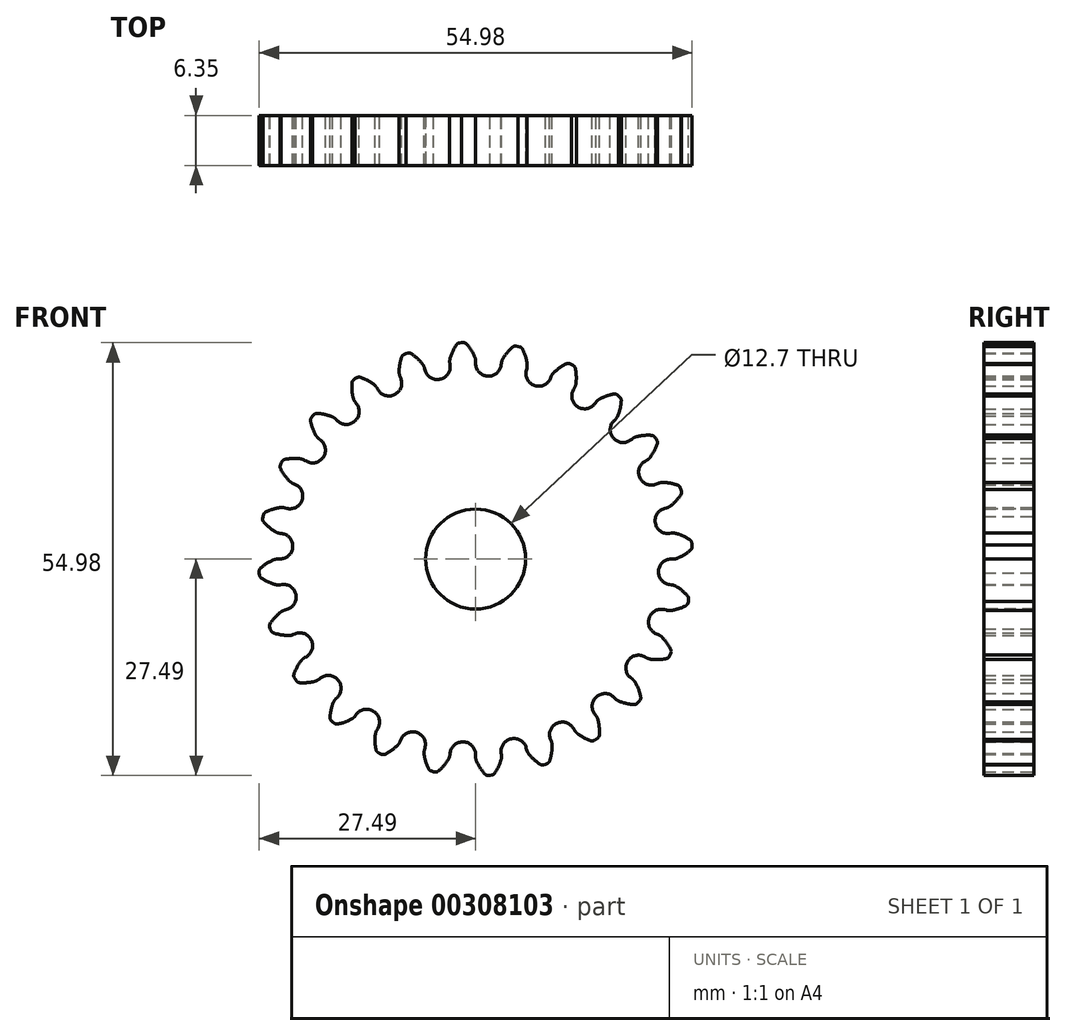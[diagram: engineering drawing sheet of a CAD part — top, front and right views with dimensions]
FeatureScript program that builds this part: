
annotation { "Feature Type Name" : "Feature", "Feature Type Description" : "" }
export const myFeature = defineFeature(function(context is Context, id is Id, definition is map)
    precondition{}
    {
        {
            var Q0;
            Q0=qCreatedBy(makeId("Front.planeOp"),FACE);
            var sketch = newSketch(context, id + "F0", { "sketchPlane" : qUnion([Q0])});
            skArc(sketch, "E0", {"start": v(-4.52, 22.84) * mm, "mid": v(-4.54, 22.84) * mm, "end": v(-4.56, 22.83) * mm});
            skArc(sketch, "E1.trimOffspring", {"start": v(-0.14, 25.74) * mm, "mid": v(-0.59, 26.56) * mm, "end": v(-1.15, 27.31) * mm});
            skLineSegment(sketch, "E2", {"start": v(0, 25.08) * mm, "end": v(0, 24.83) * mm});
            skLineSegment(sketch, "E3", {"start": v(-1.53, 27.49) * mm, "end": v(-1.8, 27.49) * mm});
            skLineSegment(sketch, "E4.MirrorCS", {"start": v(-2.07, 27.45) * mm, "end": v(-1.8, 27.49) * mm});
            skArc(sketch, "E5.MirrorCS", {"start": v(-3.22, 25.54) * mm, "mid": v(-2.89, 26.41) * mm, "end": v(-2.42, 27.23) * mm});
            skLineSegment(sketch, "E6.MirrorCS", {"start": v(-3.28, 24.87) * mm, "end": v(-3.25, 24.62) * mm});
            skPoint(sketch, "E7.orphan", {"position": v(-3, 22.68) * mm});
            skPoint(sketch, "E8.orphan", {"position": v(0, 22.88) * mm});
            skPoint(sketch, "E9.visualSharp", {"position": v(-1.3, 27.49) * mm});
            skArc(sketch, "E9.filletArc", {"start": v(-1.15, 27.31) * mm, "mid": v(-1.32, 27.44) * mm, "end": v(-1.53, 27.49) * mm});
            skPoint(sketch, "E10.visualSharp", {"position": v(-2.3, 27.42) * mm});
            skArc(sketch, "E10.filletArc", {"start": v(-2.07, 27.45) * mm, "mid": v(-2.27, 27.38) * mm, "end": v(-2.42, 27.23) * mm});
            skPoint(sketch, "E11.visualSharp", {"position": v(-3.32, 25.18) * mm});
            skArc(sketch, "E11.filletArc", {"start": v(-3.22, 25.54) * mm, "mid": v(-3.29, 25.2) * mm, "end": v(-3.28, 24.87) * mm});
            skPoint(sketch, "E12.visualSharp", {"position": v(0, 25.4) * mm});
            skArc(sketch, "E12.filletArc", {"start": v(0, 25.08) * mm, "mid": v(-0.03, 25.42) * mm, "end": v(-0.14, 25.74) * mm});
            skPoint(sketch, "E13.visualSharp", {"position": v(0, 23.28) * mm});
            skArc(sketch, "E13.filletArc", {"start": v(0, 24.83) * mm, "mid": v(0.44, 23.74) * mm, "end": v(1.5, 23.23) * mm});
            skPoint(sketch, "E14.visualSharp", {"position": v(-3.04, 23.08) * mm});
            skArc(sketch, "E14.filletArc", {"start": v(-4.52, 22.84) * mm, "mid": v(-3.53, 23.48) * mm, "end": v(-3.25, 24.62) * mm});
            skArc(sketch, "E15.1.0", {"start": v(-10.28, 20.9) * mm, "mid": v(-9.49, 21.76) * mm, "end": v(-9.5, 22.94) * mm});
            skLineSegment(sketch, "E15.1.1", {"start": v(-9.6, 23.17) * mm, "end": v(-9.5, 22.94) * mm});
            skArc(sketch, "E15.1.2", {"start": v(-9.72, 23.83) * mm, "mid": v(-9.7, 23.5) * mm, "end": v(-9.6, 23.17) * mm});
            skArc(sketch, "E15.1.3", {"start": v(-9.72, 23.83) * mm, "mid": v(-9.62, 24.77) * mm, "end": v(-9.39, 25.67) * mm});
            skArc(sketch, "E15.1.4", {"start": v(-9.1, 25.98) * mm, "mid": v(-9.28, 25.86) * mm, "end": v(-9.39, 25.67) * mm});
            skLineSegment(sketch, "E15.1.5", {"start": v(-9.1, 25.98) * mm, "end": v(-8.85, 26.08) * mm});
            skLineSegment(sketch, "E15.1.6", {"start": v(-8.6, 26.15) * mm, "end": v(-8.85, 26.08) * mm});
            skArc(sketch, "E15.1.7", {"start": v(-8.18, 26.08) * mm, "mid": v(-8.38, 26.16) * mm, "end": v(-8.6, 26.15) * mm});
            skArc(sketch, "E15.1.8", {"start": v(-6.8, 24.83) * mm, "mid": v(-7.44, 25.5) * mm, "end": v(-8.18, 26.08) * mm});
            skArc(sketch, "E15.1.9", {"start": v(-6.49, 24.23) * mm, "mid": v(-6.6, 24.54) * mm, "end": v(-6.8, 24.83) * mm});
            skLineSegment(sketch, "E15.1.10", {"start": v(-6.49, 24.23) * mm, "end": v(-6.42, 23.99) * mm});
            skArc(sketch, "E15.1.11", {"start": v(-6.42, 23.99) * mm, "mid": v(-5.72, 23.04) * mm, "end": v(-4.56, 22.83) * mm});
            skArc(sketch, "E15.2.0", {"start": v(-15.34, 17.52) * mm, "mid": v(-14.8, 18.57) * mm, "end": v(-15.12, 19.7) * mm});
            skLineSegment(sketch, "E15.2.1", {"start": v(-15.27, 19.9) * mm, "end": v(-15.12, 19.7) * mm});
            skArc(sketch, "E15.2.2", {"start": v(-15.56, 20.5) * mm, "mid": v(-15.45, 20.18) * mm, "end": v(-15.27, 19.9) * mm});
            skArc(sketch, "E15.2.3", {"start": v(-15.56, 20.5) * mm, "mid": v(-15.7, 21.43) * mm, "end": v(-15.71, 22.37) * mm});
            skArc(sketch, "E15.2.4", {"start": v(-15.52, 22.74) * mm, "mid": v(-15.65, 22.58) * mm, "end": v(-15.71, 22.37) * mm});
            skLineSegment(sketch, "E15.2.5", {"start": v(-15.52, 22.74) * mm, "end": v(-15.3, 22.9) * mm});
            skLineSegment(sketch, "E15.2.6", {"start": v(-15.07, 23.04) * mm, "end": v(-15.3, 22.9) * mm});
            skArc(sketch, "E15.2.7", {"start": v(-14.65, 23.08) * mm, "mid": v(-14.87, 23.1) * mm, "end": v(-15.07, 23.04) * mm});
            skArc(sketch, "E15.2.8", {"start": v(-12.99, 22.22) * mm, "mid": v(-13.79, 22.71) * mm, "end": v(-14.65, 23.08) * mm});
            skArc(sketch, "E15.2.9", {"start": v(-12.54, 21.72) * mm, "mid": v(-12.74, 22) * mm, "end": v(-12.99, 22.22) * mm});
            skLineSegment(sketch, "E15.2.10", {"start": v(-12.54, 21.72) * mm, "end": v(-12.41, 21.5) * mm});
            skArc(sketch, "E15.2.11", {"start": v(-12.41, 21.5) * mm, "mid": v(-11.49, 20.78) * mm, "end": v(-10.32, 20.87) * mm});
            skArc(sketch, "E15.3.0", {"start": v(-19.35, 12.95) * mm, "mid": v(-19.1, 14.1) * mm, "end": v(-19.7, 15.11) * mm});
            skLineSegment(sketch, "E15.3.1", {"start": v(-19.9, 15.26) * mm, "end": v(-19.7, 15.11) * mm});
            skArc(sketch, "E15.3.2", {"start": v(-20.34, 15.78) * mm, "mid": v(-20.15, 15.5) * mm, "end": v(-19.9, 15.26) * mm});
            skArc(sketch, "E15.3.3", {"start": v(-20.34, 15.78) * mm, "mid": v(-20.72, 16.64) * mm, "end": v(-20.97, 17.54) * mm});
            skArc(sketch, "E15.3.4", {"start": v(-20.87, 17.95) * mm, "mid": v(-20.96, 17.75) * mm, "end": v(-20.97, 17.54) * mm});
            skLineSegment(sketch, "E15.3.5", {"start": v(-20.87, 17.95) * mm, "end": v(-20.7, 18.16) * mm});
            skLineSegment(sketch, "E15.3.6", {"start": v(-20.52, 18.35) * mm, "end": v(-20.7, 18.16) * mm});
            skArc(sketch, "E15.3.7", {"start": v(-20.13, 18.5) * mm, "mid": v(-20.34, 18.47) * mm, "end": v(-20.52, 18.35) * mm});
            skArc(sketch, "E15.3.8", {"start": v(-18.3, 18.1) * mm, "mid": v(-19.2, 18.37) * mm, "end": v(-20.13, 18.5) * mm});
            skArc(sketch, "E15.3.9", {"start": v(-17.73, 17.74) * mm, "mid": v(-18, 17.95) * mm, "end": v(-18.3, 18.1) * mm});
            skLineSegment(sketch, "E15.3.10", {"start": v(-17.73, 17.74) * mm, "end": v(-17.55, 17.56) * mm});
            skArc(sketch, "E15.3.11", {"start": v(-17.55, 17.56) * mm, "mid": v(-16.47, 17.1) * mm, "end": v(-15.37, 17.5) * mm});
            skArc(sketch, "E15.4.0", {"start": v(-22.04, 7.5) * mm, "mid": v(-22.1, 8.68) * mm, "end": v(-22.94, 9.5) * mm});
            skLineSegment(sketch, "E15.4.1", {"start": v(-23.17, 9.6) * mm, "end": v(-22.94, 9.5) * mm});
            skArc(sketch, "E15.4.2", {"start": v(-23.73, 9.98) * mm, "mid": v(-23.47, 9.76) * mm, "end": v(-23.17, 9.6) * mm});
            skArc(sketch, "E15.4.3", {"start": v(-23.73, 9.98) * mm, "mid": v(-24.32, 10.7) * mm, "end": v(-24.8, 11.52) * mm});
            skArc(sketch, "E15.4.4", {"start": v(-24.8, 11.93) * mm, "mid": v(-24.85, 11.72) * mm, "end": v(-24.8, 11.52) * mm});
            skLineSegment(sketch, "E15.4.5", {"start": v(-24.8, 11.93) * mm, "end": v(-24.7, 12.18) * mm});
            skLineSegment(sketch, "E15.4.6", {"start": v(-24.57, 12.42) * mm, "end": v(-24.7, 12.18) * mm});
            skArc(sketch, "E15.4.7", {"start": v(-24.23, 12.66) * mm, "mid": v(-24.43, 12.57) * mm, "end": v(-24.57, 12.42) * mm});
            skArc(sketch, "E15.4.8", {"start": v(-22.36, 12.75) * mm, "mid": v(-23.3, 12.78) * mm, "end": v(-24.23, 12.66) * mm});
            skArc(sketch, "E15.4.9", {"start": v(-21.72, 12.55) * mm, "mid": v(-22.03, 12.68) * mm, "end": v(-22.36, 12.75) * mm});
            skLineSegment(sketch, "E15.4.10", {"start": v(-21.72, 12.55) * mm, "end": v(-21.5, 12.42) * mm});
            skArc(sketch, "E15.4.11", {"start": v(-21.5, 12.42) * mm, "mid": v(-20.34, 12.25) * mm, "end": v(-19.37, 12.92) * mm});
            skArc(sketch, "E15.5.0", {"start": v(-23.23, 1.54) * mm, "mid": v(-23.6, 2.66) * mm, "end": v(-24.62, 3.24) * mm});
            skLineSegment(sketch, "E15.5.1", {"start": v(-24.87, 3.27) * mm, "end": v(-24.62, 3.24) * mm});
            skArc(sketch, "E15.5.2", {"start": v(-25.5, 3.5) * mm, "mid": v(-25.2, 3.35) * mm, "end": v(-24.87, 3.27) * mm});
            skArc(sketch, "E15.5.3", {"start": v(-25.5, 3.5) * mm, "mid": v(-26.26, 4.05) * mm, "end": v(-26.93, 4.7) * mm});
            skArc(sketch, "E15.5.4", {"start": v(-27.05, 5.1) * mm, "mid": v(-27.03, 4.9) * mm, "end": v(-26.93, 4.7) * mm});
            skLineSegment(sketch, "E15.5.5", {"start": v(-27.05, 5.1) * mm, "end": v(-27.02, 5.37) * mm});
            skLineSegment(sketch, "E15.5.6", {"start": v(-26.95, 5.63) * mm, "end": v(-27.02, 5.37) * mm});
            skArc(sketch, "E15.5.7", {"start": v(-26.68, 5.96) * mm, "mid": v(-26.85, 5.82) * mm, "end": v(-26.95, 5.63) * mm});
            skArc(sketch, "E15.5.8", {"start": v(-24.9, 6.53) * mm, "mid": v(-25.81, 6.3) * mm, "end": v(-26.68, 5.96) * mm});
            skArc(sketch, "E15.5.9", {"start": v(-24.22, 6.5) * mm, "mid": v(-24.56, 6.55) * mm, "end": v(-24.9, 6.53) * mm});
            skLineSegment(sketch, "E15.5.10", {"start": v(-24.22, 6.5) * mm, "end": v(-23.98, 6.43) * mm});
            skArc(sketch, "E15.5.11", {"start": v(-23.98, 6.43) * mm, "mid": v(-22.81, 6.57) * mm, "end": v(-22.05, 7.47) * mm});
            skArc(sketch, "E15.6.0", {"start": v(-22.84, -4.52) * mm, "mid": v(-23.48, -3.53) * mm, "end": v(-24.62, -3.25) * mm});
            skLineSegment(sketch, "E15.6.1", {"start": v(-24.87, -3.28) * mm, "end": v(-24.62, -3.25) * mm});
            skArc(sketch, "E15.6.2", {"start": v(-25.54, -3.22) * mm, "mid": v(-25.2, -3.29) * mm, "end": v(-24.87, -3.28) * mm});
            skArc(sketch, "E15.6.3", {"start": v(-25.54, -3.22) * mm, "mid": v(-26.41, -2.89) * mm, "end": v(-27.23, -2.42) * mm});
            skArc(sketch, "E15.6.4", {"start": v(-27.45, -2.07) * mm, "mid": v(-27.38, -2.27) * mm, "end": v(-27.23, -2.42) * mm});
            skLineSegment(sketch, "E15.6.5", {"start": v(-27.45, -2.07) * mm, "end": v(-27.49, -1.8) * mm});
            skLineSegment(sketch, "E15.6.6", {"start": v(-27.49, -1.53) * mm, "end": v(-27.49, -1.8) * mm});
            skArc(sketch, "E15.6.7", {"start": v(-27.31, -1.15) * mm, "mid": v(-27.44, -1.32) * mm, "end": v(-27.49, -1.53) * mm});
            skArc(sketch, "E15.6.8", {"start": v(-25.74, -0.14) * mm, "mid": v(-26.56, -0.59) * mm, "end": v(-27.31, -1.15) * mm});
            skArc(sketch, "E15.6.9", {"start": v(-25.08, 0) * mm, "mid": v(-25.42, -0.03) * mm, "end": v(-25.74, -0.14) * mm});
            skLineSegment(sketch, "E15.6.10", {"start": v(-25.08, 0) * mm, "end": v(-24.83, 0) * mm});
            skArc(sketch, "E15.6.11", {"start": v(-24.83, 0) * mm, "mid": v(-23.74, 0.44) * mm, "end": v(-23.23, 1.5) * mm});
            skArc(sketch, "E15.7.0", {"start": v(-20.9, -10.28) * mm, "mid": v(-21.76, -9.49) * mm, "end": v(-22.94, -9.5) * mm});
            skLineSegment(sketch, "E15.7.1", {"start": v(-23.17, -9.6) * mm, "end": v(-22.94, -9.5) * mm});
            skArc(sketch, "E15.7.2", {"start": v(-23.83, -9.72) * mm, "mid": v(-23.5, -9.7) * mm, "end": v(-23.17, -9.6) * mm});
            skArc(sketch, "E15.7.3", {"start": v(-23.83, -9.72) * mm, "mid": v(-24.77, -9.62) * mm, "end": v(-25.67, -9.39) * mm});
            skArc(sketch, "E15.7.4", {"start": v(-25.98, -9.1) * mm, "mid": v(-25.86, -9.28) * mm, "end": v(-25.67, -9.39) * mm});
            skLineSegment(sketch, "E15.7.5", {"start": v(-25.98, -9.1) * mm, "end": v(-26.08, -8.85) * mm});
            skLineSegment(sketch, "E15.7.6", {"start": v(-26.15, -8.6) * mm, "end": v(-26.08, -8.85) * mm});
            skArc(sketch, "E15.7.7", {"start": v(-26.08, -8.18) * mm, "mid": v(-26.16, -8.38) * mm, "end": v(-26.15, -8.6) * mm});
            skArc(sketch, "E15.7.8", {"start": v(-24.83, -6.8) * mm, "mid": v(-25.5, -7.44) * mm, "end": v(-26.08, -8.18) * mm});
            skArc(sketch, "E15.7.9", {"start": v(-24.23, -6.49) * mm, "mid": v(-24.54, -6.6) * mm, "end": v(-24.83, -6.8) * mm});
            skLineSegment(sketch, "E15.7.10", {"start": v(-24.23, -6.49) * mm, "end": v(-23.99, -6.42) * mm});
            skArc(sketch, "E15.7.11", {"start": v(-23.99, -6.42) * mm, "mid": v(-23.04, -5.72) * mm, "end": v(-22.83, -4.56) * mm});
            skArc(sketch, "E15.8.0", {"start": v(-17.52, -15.34) * mm, "mid": v(-18.57, -14.8) * mm, "end": v(-19.7, -15.12) * mm});
            skLineSegment(sketch, "E15.8.1", {"start": v(-19.9, -15.27) * mm, "end": v(-19.7, -15.12) * mm});
            skArc(sketch, "E15.8.2", {"start": v(-20.5, -15.56) * mm, "mid": v(-20.18, -15.45) * mm, "end": v(-19.9, -15.27) * mm});
            skArc(sketch, "E15.8.3", {"start": v(-20.5, -15.56) * mm, "mid": v(-21.43, -15.7) * mm, "end": v(-22.37, -15.71) * mm});
            skArc(sketch, "E15.8.4", {"start": v(-22.74, -15.52) * mm, "mid": v(-22.58, -15.65) * mm, "end": v(-22.37, -15.71) * mm});
            skLineSegment(sketch, "E15.8.5", {"start": v(-22.74, -15.52) * mm, "end": v(-22.9, -15.3) * mm});
            skLineSegment(sketch, "E15.8.6", {"start": v(-23.04, -15.07) * mm, "end": v(-22.9, -15.3) * mm});
            skArc(sketch, "E15.8.7", {"start": v(-23.08, -14.65) * mm, "mid": v(-23.1, -14.87) * mm, "end": v(-23.04, -15.07) * mm});
            skArc(sketch, "E15.8.8", {"start": v(-22.22, -12.99) * mm, "mid": v(-22.71, -13.79) * mm, "end": v(-23.08, -14.65) * mm});
            skArc(sketch, "E15.8.9", {"start": v(-21.72, -12.54) * mm, "mid": v(-22, -12.74) * mm, "end": v(-22.22, -12.99) * mm});
            skLineSegment(sketch, "E15.8.10", {"start": v(-21.72, -12.54) * mm, "end": v(-21.5, -12.41) * mm});
            skArc(sketch, "E15.8.11", {"start": v(-21.5, -12.41) * mm, "mid": v(-20.78, -11.49) * mm, "end": v(-20.87, -10.32) * mm});
            skArc(sketch, "E15.9.0", {"start": v(-12.95, -19.35) * mm, "mid": v(-14.1, -19.1) * mm, "end": v(-15.11, -19.7) * mm});
            skLineSegment(sketch, "E15.9.1", {"start": v(-15.26, -19.9) * mm, "end": v(-15.11, -19.7) * mm});
            skArc(sketch, "E15.9.2", {"start": v(-15.78, -20.34) * mm, "mid": v(-15.5, -20.15) * mm, "end": v(-15.26, -19.9) * mm});
            skArc(sketch, "E15.9.3", {"start": v(-15.78, -20.34) * mm, "mid": v(-16.64, -20.72) * mm, "end": v(-17.54, -20.97) * mm});
            skArc(sketch, "E15.9.4", {"start": v(-17.95, -20.87) * mm, "mid": v(-17.75, -20.96) * mm, "end": v(-17.54, -20.97) * mm});
            skLineSegment(sketch, "E15.9.5", {"start": v(-17.95, -20.87) * mm, "end": v(-18.16, -20.7) * mm});
            skLineSegment(sketch, "E15.9.6", {"start": v(-18.35, -20.52) * mm, "end": v(-18.16, -20.7) * mm});
            skArc(sketch, "E15.9.7", {"start": v(-18.5, -20.13) * mm, "mid": v(-18.47, -20.34) * mm, "end": v(-18.35, -20.52) * mm});
            skArc(sketch, "E15.9.8", {"start": v(-18.1, -18.3) * mm, "mid": v(-18.37, -19.2) * mm, "end": v(-18.5, -20.13) * mm});
            skArc(sketch, "E15.9.9", {"start": v(-17.74, -17.73) * mm, "mid": v(-17.95, -18) * mm, "end": v(-18.1, -18.3) * mm});
            skLineSegment(sketch, "E15.9.10", {"start": v(-17.74, -17.73) * mm, "end": v(-17.56, -17.55) * mm});
            skArc(sketch, "E15.9.11", {"start": v(-17.56, -17.55) * mm, "mid": v(-17.1, -16.47) * mm, "end": v(-17.5, -15.37) * mm});
            skArc(sketch, "E15.10.0", {"start": v(-7.5, -22.04) * mm, "mid": v(-8.68, -22.1) * mm, "end": v(-9.5, -22.94) * mm});
            skLineSegment(sketch, "E15.10.1", {"start": v(-9.6, -23.17) * mm, "end": v(-9.5, -22.94) * mm});
            skArc(sketch, "E15.10.2", {"start": v(-9.98, -23.73) * mm, "mid": v(-9.76, -23.47) * mm, "end": v(-9.6, -23.17) * mm});
            skArc(sketch, "E15.10.3", {"start": v(-9.98, -23.73) * mm, "mid": v(-10.7, -24.32) * mm, "end": v(-11.52, -24.8) * mm});
            skArc(sketch, "E15.10.4", {"start": v(-11.93, -24.8) * mm, "mid": v(-11.72, -24.85) * mm, "end": v(-11.52, -24.8) * mm});
            skLineSegment(sketch, "E15.10.5", {"start": v(-11.93, -24.8) * mm, "end": v(-12.18, -24.7) * mm});
            skLineSegment(sketch, "E15.10.6", {"start": v(-12.42, -24.57) * mm, "end": v(-12.18, -24.7) * mm});
            skArc(sketch, "E15.10.7", {"start": v(-12.66, -24.23) * mm, "mid": v(-12.57, -24.43) * mm, "end": v(-12.42, -24.57) * mm});
            skArc(sketch, "E15.10.8", {"start": v(-12.75, -22.36) * mm, "mid": v(-12.78, -23.3) * mm, "end": v(-12.66, -24.23) * mm});
            skArc(sketch, "E15.10.9", {"start": v(-12.55, -21.72) * mm, "mid": v(-12.68, -22.03) * mm, "end": v(-12.75, -22.36) * mm});
            skLineSegment(sketch, "E15.10.10", {"start": v(-12.55, -21.72) * mm, "end": v(-12.42, -21.5) * mm});
            skArc(sketch, "E15.10.11", {"start": v(-12.42, -21.5) * mm, "mid": v(-12.25, -20.34) * mm, "end": v(-12.92, -19.37) * mm});
            skArc(sketch, "E15.11.0", {"start": v(-1.54, -23.23) * mm, "mid": v(-2.66, -23.6) * mm, "end": v(-3.24, -24.62) * mm});
            skLineSegment(sketch, "E15.11.1", {"start": v(-3.27, -24.87) * mm, "end": v(-3.24, -24.62) * mm});
            skArc(sketch, "E15.11.2", {"start": v(-3.5, -25.5) * mm, "mid": v(-3.35, -25.2) * mm, "end": v(-3.27, -24.87) * mm});
            skArc(sketch, "E15.11.3", {"start": v(-3.5, -25.5) * mm, "mid": v(-4.05, -26.26) * mm, "end": v(-4.7, -26.93) * mm});
            skArc(sketch, "E15.11.4", {"start": v(-5.1, -27.05) * mm, "mid": v(-4.9, -27.03) * mm, "end": v(-4.7, -26.93) * mm});
            skLineSegment(sketch, "E15.11.5", {"start": v(-5.1, -27.05) * mm, "end": v(-5.37, -27.02) * mm});
            skLineSegment(sketch, "E15.11.6", {"start": v(-5.63, -26.95) * mm, "end": v(-5.37, -27.02) * mm});
            skArc(sketch, "E15.11.7", {"start": v(-5.96, -26.68) * mm, "mid": v(-5.82, -26.85) * mm, "end": v(-5.63, -26.95) * mm});
            skArc(sketch, "E15.11.8", {"start": v(-6.53, -24.9) * mm, "mid": v(-6.3, -25.81) * mm, "end": v(-5.96, -26.68) * mm});
            skArc(sketch, "E15.11.9", {"start": v(-6.5, -24.22) * mm, "mid": v(-6.55, -24.56) * mm, "end": v(-6.53, -24.9) * mm});
            skLineSegment(sketch, "E15.11.10", {"start": v(-6.5, -24.22) * mm, "end": v(-6.43, -23.98) * mm});
            skArc(sketch, "E15.11.11", {"start": v(-6.43, -23.98) * mm, "mid": v(-6.57, -22.81) * mm, "end": v(-7.47, -22.05) * mm});
            skArc(sketch, "E15.12.0", {"start": v(4.52, -22.84) * mm, "mid": v(3.53, -23.48) * mm, "end": v(3.25, -24.62) * mm});
            skLineSegment(sketch, "E15.12.1", {"start": v(3.28, -24.87) * mm, "end": v(3.25, -24.62) * mm});
            skArc(sketch, "E15.12.2", {"start": v(3.22, -25.54) * mm, "mid": v(3.29, -25.2) * mm, "end": v(3.28, -24.87) * mm});
            skArc(sketch, "E15.12.3", {"start": v(3.22, -25.54) * mm, "mid": v(2.89, -26.41) * mm, "end": v(2.42, -27.23) * mm});
            skArc(sketch, "E15.12.4", {"start": v(2.07, -27.45) * mm, "mid": v(2.27, -27.38) * mm, "end": v(2.42, -27.23) * mm});
            skLineSegment(sketch, "E15.12.5", {"start": v(2.07, -27.45) * mm, "end": v(1.8, -27.49) * mm});
            skLineSegment(sketch, "E15.12.6", {"start": v(1.53, -27.49) * mm, "end": v(1.8, -27.49) * mm});
            skArc(sketch, "E15.12.7", {"start": v(1.15, -27.31) * mm, "mid": v(1.32, -27.44) * mm, "end": v(1.53, -27.49) * mm});
            skArc(sketch, "E15.12.8", {"start": v(0.14, -25.74) * mm, "mid": v(0.59, -26.56) * mm, "end": v(1.15, -27.31) * mm});
            skArc(sketch, "E15.12.9", {"start": v(0, -25.08) * mm, "mid": v(0.03, -25.42) * mm, "end": v(0.14, -25.74) * mm});
            skLineSegment(sketch, "E15.12.10", {"start": v(0, -25.08) * mm, "end": v(0, -24.83) * mm});
            skArc(sketch, "E15.12.11", {"start": v(0, -24.83) * mm, "mid": v(-0.44, -23.74) * mm, "end": v(-1.5, -23.23) * mm});
            skArc(sketch, "E15.13.0", {"start": v(10.28, -20.9) * mm, "mid": v(9.49, -21.76) * mm, "end": v(9.5, -22.94) * mm});
            skLineSegment(sketch, "E15.13.1", {"start": v(9.6, -23.17) * mm, "end": v(9.5, -22.94) * mm});
            skArc(sketch, "E15.13.2", {"start": v(9.72, -23.83) * mm, "mid": v(9.7, -23.5) * mm, "end": v(9.6, -23.17) * mm});
            skArc(sketch, "E15.13.3", {"start": v(9.72, -23.83) * mm, "mid": v(9.62, -24.77) * mm, "end": v(9.39, -25.67) * mm});
            skArc(sketch, "E15.13.4", {"start": v(9.1, -25.98) * mm, "mid": v(9.28, -25.86) * mm, "end": v(9.39, -25.67) * mm});
            skLineSegment(sketch, "E15.13.5", {"start": v(9.1, -25.98) * mm, "end": v(8.85, -26.08) * mm});
            skLineSegment(sketch, "E15.13.6", {"start": v(8.6, -26.15) * mm, "end": v(8.85, -26.08) * mm});
            skArc(sketch, "E15.13.7", {"start": v(8.18, -26.08) * mm, "mid": v(8.38, -26.16) * mm, "end": v(8.6, -26.15) * mm});
            skArc(sketch, "E15.13.8", {"start": v(6.8, -24.83) * mm, "mid": v(7.44, -25.5) * mm, "end": v(8.18, -26.08) * mm});
            skArc(sketch, "E15.13.9", {"start": v(6.49, -24.23) * mm, "mid": v(6.6, -24.54) * mm, "end": v(6.8, -24.83) * mm});
            skLineSegment(sketch, "E15.13.10", {"start": v(6.49, -24.23) * mm, "end": v(6.42, -23.99) * mm});
            skArc(sketch, "E15.13.11", {"start": v(6.42, -23.99) * mm, "mid": v(5.72, -23.04) * mm, "end": v(4.56, -22.83) * mm});
            skArc(sketch, "E15.14.0", {"start": v(15.34, -17.52) * mm, "mid": v(14.8, -18.57) * mm, "end": v(15.12, -19.7) * mm});
            skLineSegment(sketch, "E15.14.1", {"start": v(15.27, -19.9) * mm, "end": v(15.12, -19.7) * mm});
            skArc(sketch, "E15.14.2", {"start": v(15.56, -20.5) * mm, "mid": v(15.45, -20.18) * mm, "end": v(15.27, -19.9) * mm});
            skArc(sketch, "E15.14.3", {"start": v(15.56, -20.5) * mm, "mid": v(15.7, -21.43) * mm, "end": v(15.71, -22.37) * mm});
            skArc(sketch, "E15.14.4", {"start": v(15.52, -22.74) * mm, "mid": v(15.65, -22.58) * mm, "end": v(15.71, -22.37) * mm});
            skLineSegment(sketch, "E15.14.5", {"start": v(15.52, -22.74) * mm, "end": v(15.3, -22.9) * mm});
            skLineSegment(sketch, "E15.14.6", {"start": v(15.07, -23.04) * mm, "end": v(15.3, -22.9) * mm});
            skArc(sketch, "E15.14.7", {"start": v(14.65, -23.08) * mm, "mid": v(14.87, -23.1) * mm, "end": v(15.07, -23.04) * mm});
            skArc(sketch, "E15.14.8", {"start": v(12.99, -22.22) * mm, "mid": v(13.79, -22.71) * mm, "end": v(14.65, -23.08) * mm});
            skArc(sketch, "E15.14.9", {"start": v(12.54, -21.72) * mm, "mid": v(12.74, -22) * mm, "end": v(12.99, -22.22) * mm});
            skLineSegment(sketch, "E15.14.10", {"start": v(12.54, -21.72) * mm, "end": v(12.41, -21.5) * mm});
            skArc(sketch, "E15.14.11", {"start": v(12.41, -21.5) * mm, "mid": v(11.49, -20.78) * mm, "end": v(10.32, -20.87) * mm});
            skArc(sketch, "E15.15.0", {"start": v(19.35, -12.95) * mm, "mid": v(19.1, -14.1) * mm, "end": v(19.7, -15.11) * mm});
            skLineSegment(sketch, "E15.15.1", {"start": v(19.9, -15.26) * mm, "end": v(19.7, -15.11) * mm});
            skArc(sketch, "E15.15.2", {"start": v(20.34, -15.78) * mm, "mid": v(20.15, -15.5) * mm, "end": v(19.9, -15.26) * mm});
            skArc(sketch, "E15.15.3", {"start": v(20.34, -15.78) * mm, "mid": v(20.72, -16.64) * mm, "end": v(20.97, -17.54) * mm});
            skArc(sketch, "E15.15.4", {"start": v(20.87, -17.95) * mm, "mid": v(20.96, -17.75) * mm, "end": v(20.97, -17.54) * mm});
            skLineSegment(sketch, "E15.15.5", {"start": v(20.87, -17.95) * mm, "end": v(20.7, -18.16) * mm});
            skLineSegment(sketch, "E15.15.6", {"start": v(20.52, -18.35) * mm, "end": v(20.7, -18.16) * mm});
            skArc(sketch, "E15.15.7", {"start": v(20.13, -18.5) * mm, "mid": v(20.34, -18.47) * mm, "end": v(20.52, -18.35) * mm});
            skArc(sketch, "E15.15.8", {"start": v(18.3, -18.1) * mm, "mid": v(19.2, -18.37) * mm, "end": v(20.13, -18.5) * mm});
            skArc(sketch, "E15.15.9", {"start": v(17.73, -17.74) * mm, "mid": v(18, -17.95) * mm, "end": v(18.3, -18.1) * mm});
            skLineSegment(sketch, "E15.15.10", {"start": v(17.73, -17.74) * mm, "end": v(17.55, -17.56) * mm});
            skArc(sketch, "E15.15.11", {"start": v(17.55, -17.56) * mm, "mid": v(16.47, -17.1) * mm, "end": v(15.37, -17.5) * mm});
            skArc(sketch, "E15.16.0", {"start": v(22.04, -7.5) * mm, "mid": v(22.1, -8.68) * mm, "end": v(22.94, -9.5) * mm});
            skLineSegment(sketch, "E15.16.1", {"start": v(23.17, -9.6) * mm, "end": v(22.94, -9.5) * mm});
            skArc(sketch, "E15.16.2", {"start": v(23.73, -9.98) * mm, "mid": v(23.47, -9.76) * mm, "end": v(23.17, -9.6) * mm});
            skArc(sketch, "E15.16.3", {"start": v(23.73, -9.98) * mm, "mid": v(24.32, -10.7) * mm, "end": v(24.8, -11.52) * mm});
            skArc(sketch, "E15.16.4", {"start": v(24.8, -11.93) * mm, "mid": v(24.85, -11.72) * mm, "end": v(24.8, -11.52) * mm});
            skLineSegment(sketch, "E15.16.5", {"start": v(24.8, -11.93) * mm, "end": v(24.7, -12.18) * mm});
            skLineSegment(sketch, "E15.16.6", {"start": v(24.57, -12.42) * mm, "end": v(24.7, -12.18) * mm});
            skArc(sketch, "E15.16.7", {"start": v(24.23, -12.66) * mm, "mid": v(24.43, -12.57) * mm, "end": v(24.57, -12.42) * mm});
            skArc(sketch, "E15.16.8", {"start": v(22.36, -12.75) * mm, "mid": v(23.3, -12.78) * mm, "end": v(24.23, -12.66) * mm});
            skArc(sketch, "E15.16.9", {"start": v(21.72, -12.55) * mm, "mid": v(22.03, -12.68) * mm, "end": v(22.36, -12.75) * mm});
            skLineSegment(sketch, "E15.16.10", {"start": v(21.72, -12.55) * mm, "end": v(21.5, -12.42) * mm});
            skArc(sketch, "E15.16.11", {"start": v(21.5, -12.42) * mm, "mid": v(20.34, -12.25) * mm, "end": v(19.37, -12.92) * mm});
            skArc(sketch, "E15.17.0", {"start": v(23.23, -1.54) * mm, "mid": v(23.6, -2.66) * mm, "end": v(24.62, -3.24) * mm});
            skLineSegment(sketch, "E15.17.1", {"start": v(24.87, -3.27) * mm, "end": v(24.62, -3.24) * mm});
            skArc(sketch, "E15.17.2", {"start": v(25.5, -3.5) * mm, "mid": v(25.2, -3.35) * mm, "end": v(24.87, -3.27) * mm});
            skArc(sketch, "E15.17.3", {"start": v(25.5, -3.5) * mm, "mid": v(26.26, -4.05) * mm, "end": v(26.93, -4.7) * mm});
            skArc(sketch, "E15.17.4", {"start": v(27.05, -5.1) * mm, "mid": v(27.03, -4.9) * mm, "end": v(26.93, -4.7) * mm});
            skLineSegment(sketch, "E15.17.5", {"start": v(27.05, -5.1) * mm, "end": v(27.02, -5.37) * mm});
            skLineSegment(sketch, "E15.17.6", {"start": v(26.95, -5.63) * mm, "end": v(27.02, -5.37) * mm});
            skArc(sketch, "E15.17.7", {"start": v(26.68, -5.96) * mm, "mid": v(26.85, -5.82) * mm, "end": v(26.95, -5.63) * mm});
            skArc(sketch, "E15.17.8", {"start": v(24.9, -6.53) * mm, "mid": v(25.81, -6.3) * mm, "end": v(26.68, -5.96) * mm});
            skArc(sketch, "E15.17.9", {"start": v(24.22, -6.5) * mm, "mid": v(24.56, -6.55) * mm, "end": v(24.9, -6.53) * mm});
            skLineSegment(sketch, "E15.17.10", {"start": v(24.22, -6.5) * mm, "end": v(23.98, -6.43) * mm});
            skArc(sketch, "E15.17.11", {"start": v(23.98, -6.43) * mm, "mid": v(22.81, -6.57) * mm, "end": v(22.05, -7.47) * mm});
            skArc(sketch, "E15.18.0", {"start": v(22.84, 4.52) * mm, "mid": v(23.48, 3.53) * mm, "end": v(24.62, 3.25) * mm});
            skLineSegment(sketch, "E15.18.1", {"start": v(24.87, 3.28) * mm, "end": v(24.62, 3.25) * mm});
            skArc(sketch, "E15.18.2", {"start": v(25.54, 3.22) * mm, "mid": v(25.2, 3.29) * mm, "end": v(24.87, 3.28) * mm});
            skArc(sketch, "E15.18.3", {"start": v(25.54, 3.22) * mm, "mid": v(26.41, 2.89) * mm, "end": v(27.23, 2.42) * mm});
            skArc(sketch, "E15.18.4", {"start": v(27.45, 2.07) * mm, "mid": v(27.38, 2.27) * mm, "end": v(27.23, 2.42) * mm});
            skLineSegment(sketch, "E15.18.5", {"start": v(27.45, 2.07) * mm, "end": v(27.49, 1.8) * mm});
            skLineSegment(sketch, "E15.18.6", {"start": v(27.49, 1.53) * mm, "end": v(27.49, 1.8) * mm});
            skArc(sketch, "E15.18.7", {"start": v(27.31, 1.15) * mm, "mid": v(27.44, 1.32) * mm, "end": v(27.49, 1.53) * mm});
            skArc(sketch, "E15.18.8", {"start": v(25.74, 0.14) * mm, "mid": v(26.56, 0.59) * mm, "end": v(27.31, 1.15) * mm});
            skArc(sketch, "E15.18.9", {"start": v(25.08, 0) * mm, "mid": v(25.42, 0.03) * mm, "end": v(25.74, 0.14) * mm});
            skLineSegment(sketch, "E15.18.10", {"start": v(25.08, 0) * mm, "end": v(24.83, 0) * mm});
            skArc(sketch, "E15.18.11", {"start": v(24.83, 0) * mm, "mid": v(23.74, -0.44) * mm, "end": v(23.23, -1.5) * mm});
            skArc(sketch, "E15.19.0", {"start": v(20.9, 10.28) * mm, "mid": v(21.76, 9.49) * mm, "end": v(22.94, 9.5) * mm});
            skLineSegment(sketch, "E15.19.1", {"start": v(23.17, 9.6) * mm, "end": v(22.94, 9.5) * mm});
            skArc(sketch, "E15.19.2", {"start": v(23.83, 9.72) * mm, "mid": v(23.5, 9.7) * mm, "end": v(23.17, 9.6) * mm});
            skArc(sketch, "E15.19.3", {"start": v(23.83, 9.72) * mm, "mid": v(24.77, 9.62) * mm, "end": v(25.67, 9.39) * mm});
            skArc(sketch, "E15.19.4", {"start": v(25.98, 9.1) * mm, "mid": v(25.86, 9.28) * mm, "end": v(25.67, 9.39) * mm});
            skLineSegment(sketch, "E15.19.5", {"start": v(25.98, 9.1) * mm, "end": v(26.08, 8.85) * mm});
            skLineSegment(sketch, "E15.19.6", {"start": v(26.15, 8.6) * mm, "end": v(26.08, 8.85) * mm});
            skArc(sketch, "E15.19.7", {"start": v(26.08, 8.18) * mm, "mid": v(26.16, 8.38) * mm, "end": v(26.15, 8.6) * mm});
            skArc(sketch, "E15.19.8", {"start": v(24.83, 6.8) * mm, "mid": v(25.5, 7.44) * mm, "end": v(26.08, 8.18) * mm});
            skArc(sketch, "E15.19.9", {"start": v(24.23, 6.49) * mm, "mid": v(24.54, 6.6) * mm, "end": v(24.83, 6.8) * mm});
            skLineSegment(sketch, "E15.19.10", {"start": v(24.23, 6.49) * mm, "end": v(23.99, 6.42) * mm});
            skArc(sketch, "E15.19.11", {"start": v(23.99, 6.42) * mm, "mid": v(23.04, 5.72) * mm, "end": v(22.83, 4.56) * mm});
            skArc(sketch, "E15.20.0", {"start": v(17.52, 15.34) * mm, "mid": v(18.57, 14.8) * mm, "end": v(19.7, 15.12) * mm});
            skLineSegment(sketch, "E15.20.1", {"start": v(19.9, 15.27) * mm, "end": v(19.7, 15.12) * mm});
            skArc(sketch, "E15.20.2", {"start": v(20.5, 15.56) * mm, "mid": v(20.18, 15.45) * mm, "end": v(19.9, 15.27) * mm});
            skArc(sketch, "E15.20.3", {"start": v(20.5, 15.56) * mm, "mid": v(21.43, 15.7) * mm, "end": v(22.37, 15.71) * mm});
            skArc(sketch, "E15.20.4", {"start": v(22.74, 15.52) * mm, "mid": v(22.58, 15.65) * mm, "end": v(22.37, 15.71) * mm});
            skLineSegment(sketch, "E15.20.5", {"start": v(22.74, 15.52) * mm, "end": v(22.9, 15.3) * mm});
            skLineSegment(sketch, "E15.20.6", {"start": v(23.04, 15.07) * mm, "end": v(22.9, 15.3) * mm});
            skArc(sketch, "E15.20.7", {"start": v(23.08, 14.65) * mm, "mid": v(23.1, 14.87) * mm, "end": v(23.04, 15.07) * mm});
            skArc(sketch, "E15.20.8", {"start": v(22.22, 12.99) * mm, "mid": v(22.71, 13.79) * mm, "end": v(23.08, 14.65) * mm});
            skArc(sketch, "E15.20.9", {"start": v(21.72, 12.54) * mm, "mid": v(22, 12.74) * mm, "end": v(22.22, 12.99) * mm});
            skLineSegment(sketch, "E15.20.10", {"start": v(21.72, 12.54) * mm, "end": v(21.5, 12.41) * mm});
            skArc(sketch, "E15.20.11", {"start": v(21.5, 12.41) * mm, "mid": v(20.78, 11.49) * mm, "end": v(20.87, 10.32) * mm});
            skArc(sketch, "E15.21.0", {"start": v(12.95, 19.35) * mm, "mid": v(14.1, 19.1) * mm, "end": v(15.11, 19.7) * mm});
            skLineSegment(sketch, "E15.21.1", {"start": v(15.26, 19.9) * mm, "end": v(15.11, 19.7) * mm});
            skArc(sketch, "E15.21.2", {"start": v(15.78, 20.34) * mm, "mid": v(15.5, 20.15) * mm, "end": v(15.26, 19.9) * mm});
            skArc(sketch, "E15.21.3", {"start": v(15.78, 20.34) * mm, "mid": v(16.64, 20.72) * mm, "end": v(17.54, 20.97) * mm});
            skArc(sketch, "E15.21.4", {"start": v(17.95, 20.87) * mm, "mid": v(17.75, 20.96) * mm, "end": v(17.54, 20.97) * mm});
            skLineSegment(sketch, "E15.21.5", {"start": v(17.95, 20.87) * mm, "end": v(18.16, 20.7) * mm});
            skLineSegment(sketch, "E15.21.6", {"start": v(18.35, 20.52) * mm, "end": v(18.16, 20.7) * mm});
            skArc(sketch, "E15.21.7", {"start": v(18.5, 20.13) * mm, "mid": v(18.47, 20.34) * mm, "end": v(18.35, 20.52) * mm});
            skArc(sketch, "E15.21.8", {"start": v(18.1, 18.3) * mm, "mid": v(18.37, 19.2) * mm, "end": v(18.5, 20.13) * mm});
            skArc(sketch, "E15.21.9", {"start": v(17.74, 17.73) * mm, "mid": v(17.95, 18) * mm, "end": v(18.1, 18.3) * mm});
            skLineSegment(sketch, "E15.21.10", {"start": v(17.74, 17.73) * mm, "end": v(17.56, 17.55) * mm});
            skArc(sketch, "E15.21.11", {"start": v(17.56, 17.55) * mm, "mid": v(17.1, 16.47) * mm, "end": v(17.5, 15.37) * mm});
            skArc(sketch, "E15.22.0", {"start": v(7.5, 22.04) * mm, "mid": v(8.68, 22.1) * mm, "end": v(9.5, 22.94) * mm});
            skLineSegment(sketch, "E15.22.1", {"start": v(9.6, 23.17) * mm, "end": v(9.5, 22.94) * mm});
            skArc(sketch, "E15.22.2", {"start": v(9.98, 23.73) * mm, "mid": v(9.76, 23.47) * mm, "end": v(9.6, 23.17) * mm});
            skArc(sketch, "E15.22.3", {"start": v(9.98, 23.73) * mm, "mid": v(10.7, 24.32) * mm, "end": v(11.52, 24.8) * mm});
            skArc(sketch, "E15.22.4", {"start": v(11.93, 24.8) * mm, "mid": v(11.72, 24.85) * mm, "end": v(11.52, 24.8) * mm});
            skLineSegment(sketch, "E15.22.5", {"start": v(11.93, 24.8) * mm, "end": v(12.18, 24.7) * mm});
            skLineSegment(sketch, "E15.22.6", {"start": v(12.42, 24.57) * mm, "end": v(12.18, 24.7) * mm});
            skArc(sketch, "E15.22.7", {"start": v(12.66, 24.23) * mm, "mid": v(12.57, 24.43) * mm, "end": v(12.42, 24.57) * mm});
            skArc(sketch, "E15.22.8", {"start": v(12.75, 22.36) * mm, "mid": v(12.78, 23.3) * mm, "end": v(12.66, 24.23) * mm});
            skArc(sketch, "E15.22.9", {"start": v(12.55, 21.72) * mm, "mid": v(12.68, 22.03) * mm, "end": v(12.75, 22.36) * mm});
            skLineSegment(sketch, "E15.22.10", {"start": v(12.55, 21.72) * mm, "end": v(12.42, 21.5) * mm});
            skArc(sketch, "E15.22.11", {"start": v(12.42, 21.5) * mm, "mid": v(12.25, 20.34) * mm, "end": v(12.92, 19.37) * mm});
            skArc(sketch, "E15.23.0", {"start": v(1.54, 23.23) * mm, "mid": v(2.66, 23.6) * mm, "end": v(3.24, 24.62) * mm});
            skLineSegment(sketch, "E15.23.1", {"start": v(3.27, 24.87) * mm, "end": v(3.24, 24.62) * mm});
            skArc(sketch, "E15.23.2", {"start": v(3.5, 25.5) * mm, "mid": v(3.35, 25.2) * mm, "end": v(3.27, 24.87) * mm});
            skArc(sketch, "E15.23.3", {"start": v(3.5, 25.5) * mm, "mid": v(4.05, 26.26) * mm, "end": v(4.7, 26.93) * mm});
            skArc(sketch, "E15.23.4", {"start": v(5.1, 27.05) * mm, "mid": v(4.9, 27.03) * mm, "end": v(4.7, 26.93) * mm});
            skLineSegment(sketch, "E15.23.5", {"start": v(5.1, 27.05) * mm, "end": v(5.37, 27.02) * mm});
            skLineSegment(sketch, "E15.23.6", {"start": v(5.63, 26.95) * mm, "end": v(5.37, 27.02) * mm});
            skArc(sketch, "E15.23.7", {"start": v(5.96, 26.68) * mm, "mid": v(5.82, 26.85) * mm, "end": v(5.63, 26.95) * mm});
            skArc(sketch, "E15.23.8", {"start": v(6.53, 24.9) * mm, "mid": v(6.3, 25.81) * mm, "end": v(5.96, 26.68) * mm});
            skArc(sketch, "E15.23.9", {"start": v(6.5, 24.22) * mm, "mid": v(6.55, 24.56) * mm, "end": v(6.53, 24.9) * mm});
            skLineSegment(sketch, "E15.23.10", {"start": v(6.5, 24.22) * mm, "end": v(6.43, 23.98) * mm});
            skArc(sketch, "E15.23.11", {"start": v(6.43, 23.98) * mm, "mid": v(6.57, 22.81) * mm, "end": v(7.47, 22.05) * mm});
            skArc(sketch, "E16.trimOffspring", {"start": v(1.54, 23.23) * mm, "mid": v(1.52, 23.23) * mm, "end": v(1.5, 23.23) * mm});
            skArc(sketch, "E17.trimOffspring", {"start": v(7.5, 22.04) * mm, "mid": v(7.48, 22.05) * mm, "end": v(7.47, 22.05) * mm});
            skArc(sketch, "E18.trimOffspring", {"start": v(12.95, 19.35) * mm, "mid": v(12.94, 19.36) * mm, "end": v(12.92, 19.37) * mm});
            skArc(sketch, "E19.trimOffspring", {"start": v(17.52, 15.34) * mm, "mid": v(17.5, 15.35) * mm, "end": v(17.5, 15.37) * mm});
            skArc(sketch, "E20.trimOffspring", {"start": v(20.9, 10.28) * mm, "mid": v(20.88, 10.3) * mm, "end": v(20.87, 10.32) * mm});
            skArc(sketch, "E21.trimOffspring", {"start": v(22.84, 4.52) * mm, "mid": v(22.84, 4.54) * mm, "end": v(22.83, 4.56) * mm});
            skArc(sketch, "E22.trimOffspring", {"start": v(22.04, -7.5) * mm, "mid": v(22.05, -7.48) * mm, "end": v(22.05, -7.47) * mm});
            skArc(sketch, "E23.trimOffspring", {"start": v(19.35, -12.95) * mm, "mid": v(19.36, -12.94) * mm, "end": v(19.37, -12.92) * mm});
            skArc(sketch, "E24.trimOffspring", {"start": v(15.34, -17.52) * mm, "mid": v(15.35, -17.5) * mm, "end": v(15.37, -17.5) * mm});
            skArc(sketch, "E25.trimOffspring", {"start": v(23.23, -1.54) * mm, "mid": v(23.23, -1.52) * mm, "end": v(23.23, -1.5) * mm});
            skArc(sketch, "E26.trimOffspring", {"start": v(10.28, -20.9) * mm, "mid": v(10.3, -20.88) * mm, "end": v(10.32, -20.87) * mm});
            skArc(sketch, "E27.trimOffspring", {"start": v(-1.54, -23.23) * mm, "mid": v(-1.52, -23.23) * mm, "end": v(-1.5, -23.23) * mm});
            skArc(sketch, "E28.trimOffspring", {"start": v(-7.5, -22.04) * mm, "mid": v(-7.48, -22.05) * mm, "end": v(-7.47, -22.05) * mm});
            skArc(sketch, "E29.trimOffspring", {"start": v(-12.95, -19.35) * mm, "mid": v(-12.94, -19.36) * mm, "end": v(-12.92, -19.37) * mm});
            skArc(sketch, "E30.trimOffspring", {"start": v(-17.52, -15.34) * mm, "mid": v(-17.5, -15.35) * mm, "end": v(-17.5, -15.37) * mm});
            skArc(sketch, "E31.trimOffspring", {"start": v(-20.9, -10.28) * mm, "mid": v(-20.88, -10.3) * mm, "end": v(-20.87, -10.32) * mm});
            skArc(sketch, "E32.trimOffspring", {"start": v(-22.84, -4.52) * mm, "mid": v(-22.84, -4.54) * mm, "end": v(-22.83, -4.56) * mm});
            skArc(sketch, "E33.trimOffspring", {"start": v(-23.23, 1.54) * mm, "mid": v(-23.23, 1.52) * mm, "end": v(-23.23, 1.5) * mm});
            skArc(sketch, "E34.trimOffspring", {"start": v(4.52, -22.84) * mm, "mid": v(4.54, -22.84) * mm, "end": v(4.56, -22.83) * mm});
            skArc(sketch, "E35.trimOffspring", {"start": v(-22.04, 7.5) * mm, "mid": v(-22.05, 7.48) * mm, "end": v(-22.05, 7.47) * mm});
            skArc(sketch, "E36.trimOffspring", {"start": v(-19.35, 12.95) * mm, "mid": v(-19.36, 12.94) * mm, "end": v(-19.37, 12.92) * mm});
            skArc(sketch, "E37.trimOffspring", {"start": v(-15.34, 17.52) * mm, "mid": v(-15.35, 17.5) * mm, "end": v(-15.37, 17.5) * mm});
            skArc(sketch, "E38.trimOffspring", {"start": v(-10.28, 20.9) * mm, "mid": v(-10.3, 20.88) * mm, "end": v(-10.32, 20.87) * mm});
            skSolve(sketch);
        }
        {
            var Q0;
            Q0 = qSketchRegion(id + "F0", true);
            extrude(context, id + "F1", {"entities" : qUnion([Q0]), "depth" : 6.35 * mm});
        }
        {
            var Q0;
            Q0=makeQuery(id+"F1.opExtrude","CAP_FACE",FACE,{"disambiguationData":[OSD([sQuery(id+"F0.wireOp",EDGE,"E0"),sQuery(id+"F0.wireOp",EDGE,"E1.trimOffspring"),sQuery(id+"F0.wireOp",EDGE,"E2"),sQuery(id+"F0.wireOp",EDGE,"E3"),sQuery(id+"F0.wireOp",EDGE,"E4.MirrorCS"),sQuery(id+"F0.wireOp",EDGE,"E5.MirrorCS"),sQuery(id+"F0.wireOp",EDGE,"E6.MirrorCS"),sQuery(id+"F0.wireOp",EDGE,"E9.filletArc"),sQuery(id+"F0.wireOp",EDGE,"E10.filletArc"),sQuery(id+"F0.wireOp",EDGE,"E11.filletArc"),sQuery(id+"F0.wireOp",EDGE,"E12.filletArc"),sQuery(id+"F0.wireOp",EDGE,"E13.filletArc"),sQuery(id+"F0.wireOp",EDGE,"E14.filletArc"),sQuery(id+"F0.wireOp",EDGE,"E15.1.0"),sQuery(id+"F0.wireOp",EDGE,"E15.1.1"),sQuery(id+"F0.wireOp",EDGE,"E15.1.2"),sQuery(id+"F0.wireOp",EDGE,"E15.1.3"),sQuery(id+"F0.wireOp",EDGE,"E15.1.4"),sQuery(id+"F0.wireOp",EDGE,"E15.1.5"),sQuery(id+"F0.wireOp",EDGE,"E15.1.6"),sQuery(id+"F0.wireOp",EDGE,"E15.1.7"),sQuery(id+"F0.wireOp",EDGE,"E15.1.8"),sQuery(id+"F0.wireOp",EDGE,"E15.1.9"),sQuery(id+"F0.wireOp",EDGE,"E15.1.10"),sQuery(id+"F0.wireOp",EDGE,"E15.1.11"),sQuery(id+"F0.wireOp",EDGE,"E15.2.0"),sQuery(id+"F0.wireOp",EDGE,"E15.2.1"),sQuery(id+"F0.wireOp",EDGE,"E15.2.2"),sQuery(id+"F0.wireOp",EDGE,"E15.2.3"),sQuery(id+"F0.wireOp",EDGE,"E15.2.4"),sQuery(id+"F0.wireOp",EDGE,"E15.2.5"),sQuery(id+"F0.wireOp",EDGE,"E15.2.6"),sQuery(id+"F0.wireOp",EDGE,"E15.2.7"),sQuery(id+"F0.wireOp",EDGE,"E15.2.8"),sQuery(id+"F0.wireOp",EDGE,"E15.2.9"),sQuery(id+"F0.wireOp",EDGE,"E15.2.10"),sQuery(id+"F0.wireOp",EDGE,"E15.2.11"),sQuery(id+"F0.wireOp",EDGE,"E15.3.0"),sQuery(id+"F0.wireOp",EDGE,"E15.3.1"),sQuery(id+"F0.wireOp",EDGE,"E15.3.2"),sQuery(id+"F0.wireOp",EDGE,"E15.3.3"),sQuery(id+"F0.wireOp",EDGE,"E15.3.4"),sQuery(id+"F0.wireOp",EDGE,"E15.3.5"),sQuery(id+"F0.wireOp",EDGE,"E15.3.6"),sQuery(id+"F0.wireOp",EDGE,"E15.3.7"),sQuery(id+"F0.wireOp",EDGE,"E15.3.8"),sQuery(id+"F0.wireOp",EDGE,"E15.3.9"),sQuery(id+"F0.wireOp",EDGE,"E15.3.10"),sQuery(id+"F0.wireOp",EDGE,"E15.3.11"),sQuery(id+"F0.wireOp",EDGE,"E15.4.0"),sQuery(id+"F0.wireOp",EDGE,"E15.4.1"),sQuery(id+"F0.wireOp",EDGE,"E15.4.2"),sQuery(id+"F0.wireOp",EDGE,"E15.4.3"),sQuery(id+"F0.wireOp",EDGE,"E15.4.4"),sQuery(id+"F0.wireOp",EDGE,"E15.4.5"),sQuery(id+"F0.wireOp",EDGE,"E15.4.6"),sQuery(id+"F0.wireOp",EDGE,"E15.4.7"),sQuery(id+"F0.wireOp",EDGE,"E15.4.8"),sQuery(id+"F0.wireOp",EDGE,"E15.4.9"),sQuery(id+"F0.wireOp",EDGE,"E15.4.10"),sQuery(id+"F0.wireOp",EDGE,"E15.4.11"),sQuery(id+"F0.wireOp",EDGE,"E15.5.0"),sQuery(id+"F0.wireOp",EDGE,"E15.5.1"),sQuery(id+"F0.wireOp",EDGE,"E15.5.2"),sQuery(id+"F0.wireOp",EDGE,"E15.5.3"),sQuery(id+"F0.wireOp",EDGE,"E15.5.4"),sQuery(id+"F0.wireOp",EDGE,"E15.5.5"),sQuery(id+"F0.wireOp",EDGE,"E15.5.6"),sQuery(id+"F0.wireOp",EDGE,"E15.5.7"),sQuery(id+"F0.wireOp",EDGE,"E15.5.8"),sQuery(id+"F0.wireOp",EDGE,"E15.5.9"),sQuery(id+"F0.wireOp",EDGE,"E15.5.10"),sQuery(id+"F0.wireOp",EDGE,"E15.5.11"),sQuery(id+"F0.wireOp",EDGE,"E15.6.0"),sQuery(id+"F0.wireOp",EDGE,"E15.6.1"),sQuery(id+"F0.wireOp",EDGE,"E15.6.2"),sQuery(id+"F0.wireOp",EDGE,"E15.6.3"),sQuery(id+"F0.wireOp",EDGE,"E15.6.4"),sQuery(id+"F0.wireOp",EDGE,"E15.6.5"),sQuery(id+"F0.wireOp",EDGE,"E15.6.6"),sQuery(id+"F0.wireOp",EDGE,"E15.6.7"),sQuery(id+"F0.wireOp",EDGE,"E15.6.8"),sQuery(id+"F0.wireOp",EDGE,"E15.6.9"),sQuery(id+"F0.wireOp",EDGE,"E15.6.10"),sQuery(id+"F0.wireOp",EDGE,"E15.6.11"),sQuery(id+"F0.wireOp",EDGE,"E15.7.0"),sQuery(id+"F0.wireOp",EDGE,"E15.7.1"),sQuery(id+"F0.wireOp",EDGE,"E15.7.2"),sQuery(id+"F0.wireOp",EDGE,"E15.7.3"),sQuery(id+"F0.wireOp",EDGE,"E15.7.4"),sQuery(id+"F0.wireOp",EDGE,"E15.7.5"),sQuery(id+"F0.wireOp",EDGE,"E15.7.6"),sQuery(id+"F0.wireOp",EDGE,"E15.7.7"),sQuery(id+"F0.wireOp",EDGE,"E15.7.8"),sQuery(id+"F0.wireOp",EDGE,"E15.7.9"),sQuery(id+"F0.wireOp",EDGE,"E15.7.10"),sQuery(id+"F0.wireOp",EDGE,"E15.7.11"),sQuery(id+"F0.wireOp",EDGE,"E15.8.0"),sQuery(id+"F0.wireOp",EDGE,"E15.8.1"),sQuery(id+"F0.wireOp",EDGE,"E15.8.2"),sQuery(id+"F0.wireOp",EDGE,"E15.8.3"),sQuery(id+"F0.wireOp",EDGE,"E15.8.4"),sQuery(id+"F0.wireOp",EDGE,"E15.8.5"),sQuery(id+"F0.wireOp",EDGE,"E15.8.6"),sQuery(id+"F0.wireOp",EDGE,"E15.8.7"),sQuery(id+"F0.wireOp",EDGE,"E15.8.8"),sQuery(id+"F0.wireOp",EDGE,"E15.8.9"),sQuery(id+"F0.wireOp",EDGE,"E15.8.10"),sQuery(id+"F0.wireOp",EDGE,"E15.8.11"),sQuery(id+"F0.wireOp",EDGE,"E15.9.0"),sQuery(id+"F0.wireOp",EDGE,"E15.9.1"),sQuery(id+"F0.wireOp",EDGE,"E15.9.2"),sQuery(id+"F0.wireOp",EDGE,"E15.9.3"),sQuery(id+"F0.wireOp",EDGE,"E15.9.4"),sQuery(id+"F0.wireOp",EDGE,"E15.9.5"),sQuery(id+"F0.wireOp",EDGE,"E15.9.6"),sQuery(id+"F0.wireOp",EDGE,"E15.9.7"),sQuery(id+"F0.wireOp",EDGE,"E15.9.8"),sQuery(id+"F0.wireOp",EDGE,"E15.9.9"),sQuery(id+"F0.wireOp",EDGE,"E15.9.10"),sQuery(id+"F0.wireOp",EDGE,"E15.9.11"),sQuery(id+"F0.wireOp",EDGE,"E15.10.0"),sQuery(id+"F0.wireOp",EDGE,"E15.10.1"),sQuery(id+"F0.wireOp",EDGE,"E15.10.2"),sQuery(id+"F0.wireOp",EDGE,"E15.10.3"),sQuery(id+"F0.wireOp",EDGE,"E15.10.4"),sQuery(id+"F0.wireOp",EDGE,"E15.10.5"),sQuery(id+"F0.wireOp",EDGE,"E15.10.6"),sQuery(id+"F0.wireOp",EDGE,"E15.10.7"),sQuery(id+"F0.wireOp",EDGE,"E15.10.8"),sQuery(id+"F0.wireOp",EDGE,"E15.10.9"),sQuery(id+"F0.wireOp",EDGE,"E15.10.10"),sQuery(id+"F0.wireOp",EDGE,"E15.10.11"),sQuery(id+"F0.wireOp",EDGE,"E15.11.0"),sQuery(id+"F0.wireOp",EDGE,"E15.11.1"),sQuery(id+"F0.wireOp",EDGE,"E15.11.2"),sQuery(id+"F0.wireOp",EDGE,"E15.11.3"),sQuery(id+"F0.wireOp",EDGE,"E15.11.4"),sQuery(id+"F0.wireOp",EDGE,"E15.11.5"),sQuery(id+"F0.wireOp",EDGE,"E15.11.6"),sQuery(id+"F0.wireOp",EDGE,"E15.11.7"),sQuery(id+"F0.wireOp",EDGE,"E15.11.8"),sQuery(id+"F0.wireOp",EDGE,"E15.11.9"),sQuery(id+"F0.wireOp",EDGE,"E15.11.10"),sQuery(id+"F0.wireOp",EDGE,"E15.11.11"),sQuery(id+"F0.wireOp",EDGE,"E15.12.0"),sQuery(id+"F0.wireOp",EDGE,"E15.12.1"),sQuery(id+"F0.wireOp",EDGE,"E15.12.2"),sQuery(id+"F0.wireOp",EDGE,"E15.12.3"),sQuery(id+"F0.wireOp",EDGE,"E15.12.4"),sQuery(id+"F0.wireOp",EDGE,"E15.12.5"),sQuery(id+"F0.wireOp",EDGE,"E15.12.6"),sQuery(id+"F0.wireOp",EDGE,"E15.12.7"),sQuery(id+"F0.wireOp",EDGE,"E15.12.8"),sQuery(id+"F0.wireOp",EDGE,"E15.12.9"),sQuery(id+"F0.wireOp",EDGE,"E15.12.10"),sQuery(id+"F0.wireOp",EDGE,"E15.12.11"),sQuery(id+"F0.wireOp",EDGE,"E15.13.0"),sQuery(id+"F0.wireOp",EDGE,"E15.13.1"),sQuery(id+"F0.wireOp",EDGE,"E15.13.2"),sQuery(id+"F0.wireOp",EDGE,"E15.13.3"),sQuery(id+"F0.wireOp",EDGE,"E15.13.4"),sQuery(id+"F0.wireOp",EDGE,"E15.13.5"),sQuery(id+"F0.wireOp",EDGE,"E15.13.6"),sQuery(id+"F0.wireOp",EDGE,"E15.13.7"),sQuery(id+"F0.wireOp",EDGE,"E15.13.8"),sQuery(id+"F0.wireOp",EDGE,"E15.13.9"),sQuery(id+"F0.wireOp",EDGE,"E15.13.10"),sQuery(id+"F0.wireOp",EDGE,"E15.13.11"),sQuery(id+"F0.wireOp",EDGE,"E15.14.0"),sQuery(id+"F0.wireOp",EDGE,"E15.14.1"),sQuery(id+"F0.wireOp",EDGE,"E15.14.2"),sQuery(id+"F0.wireOp",EDGE,"E15.14.3"),sQuery(id+"F0.wireOp",EDGE,"E15.14.4"),sQuery(id+"F0.wireOp",EDGE,"E15.14.5"),sQuery(id+"F0.wireOp",EDGE,"E15.14.6"),sQuery(id+"F0.wireOp",EDGE,"E15.14.7"),sQuery(id+"F0.wireOp",EDGE,"E15.14.8"),sQuery(id+"F0.wireOp",EDGE,"E15.14.9"),sQuery(id+"F0.wireOp",EDGE,"E15.14.10"),sQuery(id+"F0.wireOp",EDGE,"E15.14.11"),sQuery(id+"F0.wireOp",EDGE,"E15.15.0"),sQuery(id+"F0.wireOp",EDGE,"E15.15.1"),sQuery(id+"F0.wireOp",EDGE,"E15.15.2"),sQuery(id+"F0.wireOp",EDGE,"E15.15.3"),sQuery(id+"F0.wireOp",EDGE,"E15.15.4"),sQuery(id+"F0.wireOp",EDGE,"E15.15.5"),sQuery(id+"F0.wireOp",EDGE,"E15.15.6"),sQuery(id+"F0.wireOp",EDGE,"E15.15.7"),sQuery(id+"F0.wireOp",EDGE,"E15.15.8"),sQuery(id+"F0.wireOp",EDGE,"E15.15.9"),sQuery(id+"F0.wireOp",EDGE,"E15.15.10"),sQuery(id+"F0.wireOp",EDGE,"E15.15.11"),sQuery(id+"F0.wireOp",EDGE,"E15.16.0"),sQuery(id+"F0.wireOp",EDGE,"E15.16.1"),sQuery(id+"F0.wireOp",EDGE,"E15.16.2"),sQuery(id+"F0.wireOp",EDGE,"E15.16.3"),sQuery(id+"F0.wireOp",EDGE,"E15.16.4"),sQuery(id+"F0.wireOp",EDGE,"E15.16.5"),sQuery(id+"F0.wireOp",EDGE,"E15.16.6"),sQuery(id+"F0.wireOp",EDGE,"E15.16.7"),sQuery(id+"F0.wireOp",EDGE,"E15.16.8"),sQuery(id+"F0.wireOp",EDGE,"E15.16.9"),sQuery(id+"F0.wireOp",EDGE,"E15.16.10"),sQuery(id+"F0.wireOp",EDGE,"E15.16.11"),sQuery(id+"F0.wireOp",EDGE,"E15.17.0"),sQuery(id+"F0.wireOp",EDGE,"E15.17.1"),sQuery(id+"F0.wireOp",EDGE,"E15.17.2"),sQuery(id+"F0.wireOp",EDGE,"E15.17.3"),sQuery(id+"F0.wireOp",EDGE,"E15.17.4"),sQuery(id+"F0.wireOp",EDGE,"E15.17.5"),sQuery(id+"F0.wireOp",EDGE,"E15.17.6"),sQuery(id+"F0.wireOp",EDGE,"E15.17.7"),sQuery(id+"F0.wireOp",EDGE,"E15.17.8"),sQuery(id+"F0.wireOp",EDGE,"E15.17.9"),sQuery(id+"F0.wireOp",EDGE,"E15.17.10"),sQuery(id+"F0.wireOp",EDGE,"E15.17.11"),sQuery(id+"F0.wireOp",EDGE,"E15.18.0"),sQuery(id+"F0.wireOp",EDGE,"E15.18.1"),sQuery(id+"F0.wireOp",EDGE,"E15.18.2"),sQuery(id+"F0.wireOp",EDGE,"E15.18.3"),sQuery(id+"F0.wireOp",EDGE,"E15.18.4"),sQuery(id+"F0.wireOp",EDGE,"E15.18.5"),sQuery(id+"F0.wireOp",EDGE,"E15.18.6"),sQuery(id+"F0.wireOp",EDGE,"E15.18.7"),sQuery(id+"F0.wireOp",EDGE,"E15.18.8"),sQuery(id+"F0.wireOp",EDGE,"E15.18.9"),sQuery(id+"F0.wireOp",EDGE,"E15.18.10"),sQuery(id+"F0.wireOp",EDGE,"E15.18.11"),sQuery(id+"F0.wireOp",EDGE,"E15.19.0"),sQuery(id+"F0.wireOp",EDGE,"E15.19.1"),sQuery(id+"F0.wireOp",EDGE,"E15.19.2"),sQuery(id+"F0.wireOp",EDGE,"E15.19.3"),sQuery(id+"F0.wireOp",EDGE,"E15.19.4"),sQuery(id+"F0.wireOp",EDGE,"E15.19.5"),sQuery(id+"F0.wireOp",EDGE,"E15.19.6"),sQuery(id+"F0.wireOp",EDGE,"E15.19.7"),sQuery(id+"F0.wireOp",EDGE,"E15.19.8"),sQuery(id+"F0.wireOp",EDGE,"E15.19.9"),sQuery(id+"F0.wireOp",EDGE,"E15.19.10"),sQuery(id+"F0.wireOp",EDGE,"E15.19.11"),sQuery(id+"F0.wireOp",EDGE,"E15.20.0"),sQuery(id+"F0.wireOp",EDGE,"E15.20.1"),sQuery(id+"F0.wireOp",EDGE,"E15.20.2"),sQuery(id+"F0.wireOp",EDGE,"E15.20.3"),sQuery(id+"F0.wireOp",EDGE,"E15.20.4"),sQuery(id+"F0.wireOp",EDGE,"E15.20.5"),sQuery(id+"F0.wireOp",EDGE,"E15.20.6"),sQuery(id+"F0.wireOp",EDGE,"E15.20.7"),sQuery(id+"F0.wireOp",EDGE,"E15.20.8"),sQuery(id+"F0.wireOp",EDGE,"E15.20.9"),sQuery(id+"F0.wireOp",EDGE,"E15.20.10"),sQuery(id+"F0.wireOp",EDGE,"E15.20.11"),sQuery(id+"F0.wireOp",EDGE,"E15.21.0"),sQuery(id+"F0.wireOp",EDGE,"E15.21.1"),sQuery(id+"F0.wireOp",EDGE,"E15.21.2"),sQuery(id+"F0.wireOp",EDGE,"E15.21.3"),sQuery(id+"F0.wireOp",EDGE,"E15.21.4"),sQuery(id+"F0.wireOp",EDGE,"E15.21.5"),sQuery(id+"F0.wireOp",EDGE,"E15.21.6"),sQuery(id+"F0.wireOp",EDGE,"E15.21.7"),sQuery(id+"F0.wireOp",EDGE,"E15.21.8"),sQuery(id+"F0.wireOp",EDGE,"E15.21.9"),sQuery(id+"F0.wireOp",EDGE,"E15.21.10"),sQuery(id+"F0.wireOp",EDGE,"E15.21.11"),sQuery(id+"F0.wireOp",EDGE,"E15.22.0"),sQuery(id+"F0.wireOp",EDGE,"E15.22.1"),sQuery(id+"F0.wireOp",EDGE,"E15.22.2"),sQuery(id+"F0.wireOp",EDGE,"E15.22.3"),sQuery(id+"F0.wireOp",EDGE,"E15.22.4"),sQuery(id+"F0.wireOp",EDGE,"E15.22.5"),sQuery(id+"F0.wireOp",EDGE,"E15.22.6"),sQuery(id+"F0.wireOp",EDGE,"E15.22.7"),sQuery(id+"F0.wireOp",EDGE,"E15.22.8"),sQuery(id+"F0.wireOp",EDGE,"E15.22.9"),sQuery(id+"F0.wireOp",EDGE,"E15.22.10"),sQuery(id+"F0.wireOp",EDGE,"E15.22.11"),sQuery(id+"F0.wireOp",EDGE,"E15.23.0"),sQuery(id+"F0.wireOp",EDGE,"E15.23.1"),sQuery(id+"F0.wireOp",EDGE,"E15.23.2"),sQuery(id+"F0.wireOp",EDGE,"E15.23.3"),sQuery(id+"F0.wireOp",EDGE,"E15.23.4"),sQuery(id+"F0.wireOp",EDGE,"E15.23.5"),sQuery(id+"F0.wireOp",EDGE,"E15.23.6"),sQuery(id+"F0.wireOp",EDGE,"E15.23.7"),sQuery(id+"F0.wireOp",EDGE,"E15.23.8"),sQuery(id+"F0.wireOp",EDGE,"E15.23.9"),sQuery(id+"F0.wireOp",EDGE,"E15.23.10"),sQuery(id+"F0.wireOp",EDGE,"E15.23.11"),sQuery(id+"F0.wireOp",EDGE,"E16.trimOffspring"),sQuery(id+"F0.wireOp",EDGE,"E17.trimOffspring"),sQuery(id+"F0.wireOp",EDGE,"E18.trimOffspring"),sQuery(id+"F0.wireOp",EDGE,"E19.trimOffspring"),sQuery(id+"F0.wireOp",EDGE,"E20.trimOffspring"),sQuery(id+"F0.wireOp",EDGE,"E21.trimOffspring"),sQuery(id+"F0.wireOp",EDGE,"E22.trimOffspring"),sQuery(id+"F0.wireOp",EDGE,"E23.trimOffspring"),sQuery(id+"F0.wireOp",EDGE,"E24.trimOffspring"),sQuery(id+"F0.wireOp",EDGE,"E25.trimOffspring"),sQuery(id+"F0.wireOp",EDGE,"E26.trimOffspring"),sQuery(id+"F0.wireOp",EDGE,"E27.trimOffspring"),sQuery(id+"F0.wireOp",EDGE,"E28.trimOffspring"),sQuery(id+"F0.wireOp",EDGE,"E29.trimOffspring"),sQuery(id+"F0.wireOp",EDGE,"E30.trimOffspring"),sQuery(id+"F0.wireOp",EDGE,"E31.trimOffspring"),sQuery(id+"F0.wireOp",EDGE,"E32.trimOffspring"),sQuery(id+"F0.wireOp",EDGE,"E33.trimOffspring"),sQuery(id+"F0.wireOp",EDGE,"E34.trimOffspring"),sQuery(id+"F0.wireOp",EDGE,"E35.trimOffspring"),sQuery(id+"F0.wireOp",EDGE,"E36.trimOffspring"),sQuery(id+"F0.wireOp",EDGE,"E37.trimOffspring"),sQuery(id+"F0.wireOp",EDGE,"E38.trimOffspring")])],"isStart":false});
            var sketch = newSketch(context, id + "F2", { "sketchPlane" : qUnion([Q0])});
            skPoint(sketch, "E39", {"position": v(0, 0) * mm});
            skSolve(sketch);
        }
        {
            var Q0;
            Q0=sQuery(id+"F2.wireOp",VERTEX,"E39");
            var Q1;
            Q1=makeQuery(id+"F1.opExtrude","SWEPT_BODY",BODY,{"disambiguationData":[OSD([sQuery(id+"F0.wireOp",EDGE,"E0"),sQuery(id+"F0.wireOp",EDGE,"E1.trimOffspring"),sQuery(id+"F0.wireOp",EDGE,"E2"),sQuery(id+"F0.wireOp",EDGE,"E3"),sQuery(id+"F0.wireOp",EDGE,"E4.MirrorCS"),sQuery(id+"F0.wireOp",EDGE,"E5.MirrorCS"),sQuery(id+"F0.wireOp",EDGE,"E6.MirrorCS"),sQuery(id+"F0.wireOp",EDGE,"E9.filletArc"),sQuery(id+"F0.wireOp",EDGE,"E10.filletArc"),sQuery(id+"F0.wireOp",EDGE,"E11.filletArc"),sQuery(id+"F0.wireOp",EDGE,"E12.filletArc"),sQuery(id+"F0.wireOp",EDGE,"E13.filletArc"),sQuery(id+"F0.wireOp",EDGE,"E14.filletArc"),sQuery(id+"F0.wireOp",EDGE,"E15.1.0"),sQuery(id+"F0.wireOp",EDGE,"E15.1.1"),sQuery(id+"F0.wireOp",EDGE,"E15.1.2"),sQuery(id+"F0.wireOp",EDGE,"E15.1.3"),sQuery(id+"F0.wireOp",EDGE,"E15.1.4"),sQuery(id+"F0.wireOp",EDGE,"E15.1.5"),sQuery(id+"F0.wireOp",EDGE,"E15.1.6"),sQuery(id+"F0.wireOp",EDGE,"E15.1.7"),sQuery(id+"F0.wireOp",EDGE,"E15.1.8"),sQuery(id+"F0.wireOp",EDGE,"E15.1.9"),sQuery(id+"F0.wireOp",EDGE,"E15.1.10"),sQuery(id+"F0.wireOp",EDGE,"E15.1.11"),sQuery(id+"F0.wireOp",EDGE,"E15.2.0"),sQuery(id+"F0.wireOp",EDGE,"E15.2.1"),sQuery(id+"F0.wireOp",EDGE,"E15.2.2"),sQuery(id+"F0.wireOp",EDGE,"E15.2.3"),sQuery(id+"F0.wireOp",EDGE,"E15.2.4"),sQuery(id+"F0.wireOp",EDGE,"E15.2.5"),sQuery(id+"F0.wireOp",EDGE,"E15.2.6"),sQuery(id+"F0.wireOp",EDGE,"E15.2.7"),sQuery(id+"F0.wireOp",EDGE,"E15.2.8"),sQuery(id+"F0.wireOp",EDGE,"E15.2.9"),sQuery(id+"F0.wireOp",EDGE,"E15.2.10"),sQuery(id+"F0.wireOp",EDGE,"E15.2.11"),sQuery(id+"F0.wireOp",EDGE,"E15.3.0"),sQuery(id+"F0.wireOp",EDGE,"E15.3.1"),sQuery(id+"F0.wireOp",EDGE,"E15.3.2"),sQuery(id+"F0.wireOp",EDGE,"E15.3.3"),sQuery(id+"F0.wireOp",EDGE,"E15.3.4"),sQuery(id+"F0.wireOp",EDGE,"E15.3.5"),sQuery(id+"F0.wireOp",EDGE,"E15.3.6"),sQuery(id+"F0.wireOp",EDGE,"E15.3.7"),sQuery(id+"F0.wireOp",EDGE,"E15.3.8"),sQuery(id+"F0.wireOp",EDGE,"E15.3.9"),sQuery(id+"F0.wireOp",EDGE,"E15.3.10"),sQuery(id+"F0.wireOp",EDGE,"E15.3.11"),sQuery(id+"F0.wireOp",EDGE,"E15.4.0"),sQuery(id+"F0.wireOp",EDGE,"E15.4.1"),sQuery(id+"F0.wireOp",EDGE,"E15.4.2"),sQuery(id+"F0.wireOp",EDGE,"E15.4.3"),sQuery(id+"F0.wireOp",EDGE,"E15.4.4"),sQuery(id+"F0.wireOp",EDGE,"E15.4.5"),sQuery(id+"F0.wireOp",EDGE,"E15.4.6"),sQuery(id+"F0.wireOp",EDGE,"E15.4.7"),sQuery(id+"F0.wireOp",EDGE,"E15.4.8"),sQuery(id+"F0.wireOp",EDGE,"E15.4.9"),sQuery(id+"F0.wireOp",EDGE,"E15.4.10"),sQuery(id+"F0.wireOp",EDGE,"E15.4.11"),sQuery(id+"F0.wireOp",EDGE,"E15.5.0"),sQuery(id+"F0.wireOp",EDGE,"E15.5.1"),sQuery(id+"F0.wireOp",EDGE,"E15.5.2"),sQuery(id+"F0.wireOp",EDGE,"E15.5.3"),sQuery(id+"F0.wireOp",EDGE,"E15.5.4"),sQuery(id+"F0.wireOp",EDGE,"E15.5.5"),sQuery(id+"F0.wireOp",EDGE,"E15.5.6"),sQuery(id+"F0.wireOp",EDGE,"E15.5.7"),sQuery(id+"F0.wireOp",EDGE,"E15.5.8"),sQuery(id+"F0.wireOp",EDGE,"E15.5.9"),sQuery(id+"F0.wireOp",EDGE,"E15.5.10"),sQuery(id+"F0.wireOp",EDGE,"E15.5.11"),sQuery(id+"F0.wireOp",EDGE,"E15.6.0"),sQuery(id+"F0.wireOp",EDGE,"E15.6.1"),sQuery(id+"F0.wireOp",EDGE,"E15.6.2"),sQuery(id+"F0.wireOp",EDGE,"E15.6.3"),sQuery(id+"F0.wireOp",EDGE,"E15.6.4"),sQuery(id+"F0.wireOp",EDGE,"E15.6.5"),sQuery(id+"F0.wireOp",EDGE,"E15.6.6"),sQuery(id+"F0.wireOp",EDGE,"E15.6.7"),sQuery(id+"F0.wireOp",EDGE,"E15.6.8"),sQuery(id+"F0.wireOp",EDGE,"E15.6.9"),sQuery(id+"F0.wireOp",EDGE,"E15.6.10"),sQuery(id+"F0.wireOp",EDGE,"E15.6.11"),sQuery(id+"F0.wireOp",EDGE,"E15.7.0"),sQuery(id+"F0.wireOp",EDGE,"E15.7.1"),sQuery(id+"F0.wireOp",EDGE,"E15.7.2"),sQuery(id+"F0.wireOp",EDGE,"E15.7.3"),sQuery(id+"F0.wireOp",EDGE,"E15.7.4"),sQuery(id+"F0.wireOp",EDGE,"E15.7.5"),sQuery(id+"F0.wireOp",EDGE,"E15.7.6"),sQuery(id+"F0.wireOp",EDGE,"E15.7.7"),sQuery(id+"F0.wireOp",EDGE,"E15.7.8"),sQuery(id+"F0.wireOp",EDGE,"E15.7.9"),sQuery(id+"F0.wireOp",EDGE,"E15.7.10"),sQuery(id+"F0.wireOp",EDGE,"E15.7.11"),sQuery(id+"F0.wireOp",EDGE,"E15.8.0"),sQuery(id+"F0.wireOp",EDGE,"E15.8.1"),sQuery(id+"F0.wireOp",EDGE,"E15.8.2"),sQuery(id+"F0.wireOp",EDGE,"E15.8.3"),sQuery(id+"F0.wireOp",EDGE,"E15.8.4"),sQuery(id+"F0.wireOp",EDGE,"E15.8.5"),sQuery(id+"F0.wireOp",EDGE,"E15.8.6"),sQuery(id+"F0.wireOp",EDGE,"E15.8.7"),sQuery(id+"F0.wireOp",EDGE,"E15.8.8"),sQuery(id+"F0.wireOp",EDGE,"E15.8.9"),sQuery(id+"F0.wireOp",EDGE,"E15.8.10"),sQuery(id+"F0.wireOp",EDGE,"E15.8.11"),sQuery(id+"F0.wireOp",EDGE,"E15.9.0"),sQuery(id+"F0.wireOp",EDGE,"E15.9.1"),sQuery(id+"F0.wireOp",EDGE,"E15.9.2"),sQuery(id+"F0.wireOp",EDGE,"E15.9.3"),sQuery(id+"F0.wireOp",EDGE,"E15.9.4"),sQuery(id+"F0.wireOp",EDGE,"E15.9.5"),sQuery(id+"F0.wireOp",EDGE,"E15.9.6"),sQuery(id+"F0.wireOp",EDGE,"E15.9.7"),sQuery(id+"F0.wireOp",EDGE,"E15.9.8"),sQuery(id+"F0.wireOp",EDGE,"E15.9.9"),sQuery(id+"F0.wireOp",EDGE,"E15.9.10"),sQuery(id+"F0.wireOp",EDGE,"E15.9.11"),sQuery(id+"F0.wireOp",EDGE,"E15.10.0"),sQuery(id+"F0.wireOp",EDGE,"E15.10.1"),sQuery(id+"F0.wireOp",EDGE,"E15.10.2"),sQuery(id+"F0.wireOp",EDGE,"E15.10.3"),sQuery(id+"F0.wireOp",EDGE,"E15.10.4"),sQuery(id+"F0.wireOp",EDGE,"E15.10.5"),sQuery(id+"F0.wireOp",EDGE,"E15.10.6"),sQuery(id+"F0.wireOp",EDGE,"E15.10.7"),sQuery(id+"F0.wireOp",EDGE,"E15.10.8"),sQuery(id+"F0.wireOp",EDGE,"E15.10.9"),sQuery(id+"F0.wireOp",EDGE,"E15.10.10"),sQuery(id+"F0.wireOp",EDGE,"E15.10.11"),sQuery(id+"F0.wireOp",EDGE,"E15.11.0"),sQuery(id+"F0.wireOp",EDGE,"E15.11.1"),sQuery(id+"F0.wireOp",EDGE,"E15.11.2"),sQuery(id+"F0.wireOp",EDGE,"E15.11.3"),sQuery(id+"F0.wireOp",EDGE,"E15.11.4"),sQuery(id+"F0.wireOp",EDGE,"E15.11.5"),sQuery(id+"F0.wireOp",EDGE,"E15.11.6"),sQuery(id+"F0.wireOp",EDGE,"E15.11.7"),sQuery(id+"F0.wireOp",EDGE,"E15.11.8"),sQuery(id+"F0.wireOp",EDGE,"E15.11.9"),sQuery(id+"F0.wireOp",EDGE,"E15.11.10"),sQuery(id+"F0.wireOp",EDGE,"E15.11.11"),sQuery(id+"F0.wireOp",EDGE,"E15.12.0"),sQuery(id+"F0.wireOp",EDGE,"E15.12.1"),sQuery(id+"F0.wireOp",EDGE,"E15.12.2"),sQuery(id+"F0.wireOp",EDGE,"E15.12.3"),sQuery(id+"F0.wireOp",EDGE,"E15.12.4"),sQuery(id+"F0.wireOp",EDGE,"E15.12.5"),sQuery(id+"F0.wireOp",EDGE,"E15.12.6"),sQuery(id+"F0.wireOp",EDGE,"E15.12.7"),sQuery(id+"F0.wireOp",EDGE,"E15.12.8"),sQuery(id+"F0.wireOp",EDGE,"E15.12.9"),sQuery(id+"F0.wireOp",EDGE,"E15.12.10"),sQuery(id+"F0.wireOp",EDGE,"E15.12.11"),sQuery(id+"F0.wireOp",EDGE,"E15.13.0"),sQuery(id+"F0.wireOp",EDGE,"E15.13.1"),sQuery(id+"F0.wireOp",EDGE,"E15.13.2"),sQuery(id+"F0.wireOp",EDGE,"E15.13.3"),sQuery(id+"F0.wireOp",EDGE,"E15.13.4"),sQuery(id+"F0.wireOp",EDGE,"E15.13.5"),sQuery(id+"F0.wireOp",EDGE,"E15.13.6"),sQuery(id+"F0.wireOp",EDGE,"E15.13.7"),sQuery(id+"F0.wireOp",EDGE,"E15.13.8"),sQuery(id+"F0.wireOp",EDGE,"E15.13.9"),sQuery(id+"F0.wireOp",EDGE,"E15.13.10"),sQuery(id+"F0.wireOp",EDGE,"E15.13.11"),sQuery(id+"F0.wireOp",EDGE,"E15.14.0"),sQuery(id+"F0.wireOp",EDGE,"E15.14.1"),sQuery(id+"F0.wireOp",EDGE,"E15.14.2"),sQuery(id+"F0.wireOp",EDGE,"E15.14.3"),sQuery(id+"F0.wireOp",EDGE,"E15.14.4"),sQuery(id+"F0.wireOp",EDGE,"E15.14.5"),sQuery(id+"F0.wireOp",EDGE,"E15.14.6"),sQuery(id+"F0.wireOp",EDGE,"E15.14.7"),sQuery(id+"F0.wireOp",EDGE,"E15.14.8"),sQuery(id+"F0.wireOp",EDGE,"E15.14.9"),sQuery(id+"F0.wireOp",EDGE,"E15.14.10"),sQuery(id+"F0.wireOp",EDGE,"E15.14.11"),sQuery(id+"F0.wireOp",EDGE,"E15.15.0"),sQuery(id+"F0.wireOp",EDGE,"E15.15.1"),sQuery(id+"F0.wireOp",EDGE,"E15.15.2"),sQuery(id+"F0.wireOp",EDGE,"E15.15.3"),sQuery(id+"F0.wireOp",EDGE,"E15.15.4"),sQuery(id+"F0.wireOp",EDGE,"E15.15.5"),sQuery(id+"F0.wireOp",EDGE,"E15.15.6"),sQuery(id+"F0.wireOp",EDGE,"E15.15.7"),sQuery(id+"F0.wireOp",EDGE,"E15.15.8"),sQuery(id+"F0.wireOp",EDGE,"E15.15.9"),sQuery(id+"F0.wireOp",EDGE,"E15.15.10"),sQuery(id+"F0.wireOp",EDGE,"E15.15.11"),sQuery(id+"F0.wireOp",EDGE,"E15.16.0"),sQuery(id+"F0.wireOp",EDGE,"E15.16.1"),sQuery(id+"F0.wireOp",EDGE,"E15.16.2"),sQuery(id+"F0.wireOp",EDGE,"E15.16.3"),sQuery(id+"F0.wireOp",EDGE,"E15.16.4"),sQuery(id+"F0.wireOp",EDGE,"E15.16.5"),sQuery(id+"F0.wireOp",EDGE,"E15.16.6"),sQuery(id+"F0.wireOp",EDGE,"E15.16.7"),sQuery(id+"F0.wireOp",EDGE,"E15.16.8"),sQuery(id+"F0.wireOp",EDGE,"E15.16.9"),sQuery(id+"F0.wireOp",EDGE,"E15.16.10"),sQuery(id+"F0.wireOp",EDGE,"E15.16.11"),sQuery(id+"F0.wireOp",EDGE,"E15.17.0"),sQuery(id+"F0.wireOp",EDGE,"E15.17.1"),sQuery(id+"F0.wireOp",EDGE,"E15.17.2"),sQuery(id+"F0.wireOp",EDGE,"E15.17.3"),sQuery(id+"F0.wireOp",EDGE,"E15.17.4"),sQuery(id+"F0.wireOp",EDGE,"E15.17.5"),sQuery(id+"F0.wireOp",EDGE,"E15.17.6"),sQuery(id+"F0.wireOp",EDGE,"E15.17.7"),sQuery(id+"F0.wireOp",EDGE,"E15.17.8"),sQuery(id+"F0.wireOp",EDGE,"E15.17.9"),sQuery(id+"F0.wireOp",EDGE,"E15.17.10"),sQuery(id+"F0.wireOp",EDGE,"E15.17.11"),sQuery(id+"F0.wireOp",EDGE,"E15.18.0"),sQuery(id+"F0.wireOp",EDGE,"E15.18.1"),sQuery(id+"F0.wireOp",EDGE,"E15.18.2"),sQuery(id+"F0.wireOp",EDGE,"E15.18.3"),sQuery(id+"F0.wireOp",EDGE,"E15.18.4"),sQuery(id+"F0.wireOp",EDGE,"E15.18.5"),sQuery(id+"F0.wireOp",EDGE,"E15.18.6"),sQuery(id+"F0.wireOp",EDGE,"E15.18.7"),sQuery(id+"F0.wireOp",EDGE,"E15.18.8"),sQuery(id+"F0.wireOp",EDGE,"E15.18.9"),sQuery(id+"F0.wireOp",EDGE,"E15.18.10"),sQuery(id+"F0.wireOp",EDGE,"E15.18.11"),sQuery(id+"F0.wireOp",EDGE,"E15.19.0"),sQuery(id+"F0.wireOp",EDGE,"E15.19.1"),sQuery(id+"F0.wireOp",EDGE,"E15.19.2"),sQuery(id+"F0.wireOp",EDGE,"E15.19.3"),sQuery(id+"F0.wireOp",EDGE,"E15.19.4"),sQuery(id+"F0.wireOp",EDGE,"E15.19.5"),sQuery(id+"F0.wireOp",EDGE,"E15.19.6"),sQuery(id+"F0.wireOp",EDGE,"E15.19.7"),sQuery(id+"F0.wireOp",EDGE,"E15.19.8"),sQuery(id+"F0.wireOp",EDGE,"E15.19.9"),sQuery(id+"F0.wireOp",EDGE,"E15.19.10"),sQuery(id+"F0.wireOp",EDGE,"E15.19.11"),sQuery(id+"F0.wireOp",EDGE,"E15.20.0"),sQuery(id+"F0.wireOp",EDGE,"E15.20.1"),sQuery(id+"F0.wireOp",EDGE,"E15.20.2"),sQuery(id+"F0.wireOp",EDGE,"E15.20.3"),sQuery(id+"F0.wireOp",EDGE,"E15.20.4"),sQuery(id+"F0.wireOp",EDGE,"E15.20.5"),sQuery(id+"F0.wireOp",EDGE,"E15.20.6"),sQuery(id+"F0.wireOp",EDGE,"E15.20.7"),sQuery(id+"F0.wireOp",EDGE,"E15.20.8"),sQuery(id+"F0.wireOp",EDGE,"E15.20.9"),sQuery(id+"F0.wireOp",EDGE,"E15.20.10"),sQuery(id+"F0.wireOp",EDGE,"E15.20.11"),sQuery(id+"F0.wireOp",EDGE,"E15.21.0"),sQuery(id+"F0.wireOp",EDGE,"E15.21.1"),sQuery(id+"F0.wireOp",EDGE,"E15.21.2"),sQuery(id+"F0.wireOp",EDGE,"E15.21.3"),sQuery(id+"F0.wireOp",EDGE,"E15.21.4"),sQuery(id+"F0.wireOp",EDGE,"E15.21.5"),sQuery(id+"F0.wireOp",EDGE,"E15.21.6"),sQuery(id+"F0.wireOp",EDGE,"E15.21.7"),sQuery(id+"F0.wireOp",EDGE,"E15.21.8"),sQuery(id+"F0.wireOp",EDGE,"E15.21.9"),sQuery(id+"F0.wireOp",EDGE,"E15.21.10"),sQuery(id+"F0.wireOp",EDGE,"E15.21.11"),sQuery(id+"F0.wireOp",EDGE,"E15.22.0"),sQuery(id+"F0.wireOp",EDGE,"E15.22.1"),sQuery(id+"F0.wireOp",EDGE,"E15.22.2"),sQuery(id+"F0.wireOp",EDGE,"E15.22.3"),sQuery(id+"F0.wireOp",EDGE,"E15.22.4"),sQuery(id+"F0.wireOp",EDGE,"E15.22.5"),sQuery(id+"F0.wireOp",EDGE,"E15.22.6"),sQuery(id+"F0.wireOp",EDGE,"E15.22.7"),sQuery(id+"F0.wireOp",EDGE,"E15.22.8"),sQuery(id+"F0.wireOp",EDGE,"E15.22.9"),sQuery(id+"F0.wireOp",EDGE,"E15.22.10"),sQuery(id+"F0.wireOp",EDGE,"E15.22.11"),sQuery(id+"F0.wireOp",EDGE,"E15.23.0"),sQuery(id+"F0.wireOp",EDGE,"E15.23.1"),sQuery(id+"F0.wireOp",EDGE,"E15.23.2"),sQuery(id+"F0.wireOp",EDGE,"E15.23.3"),sQuery(id+"F0.wireOp",EDGE,"E15.23.4"),sQuery(id+"F0.wireOp",EDGE,"E15.23.5"),sQuery(id+"F0.wireOp",EDGE,"E15.23.6"),sQuery(id+"F0.wireOp",EDGE,"E15.23.7"),sQuery(id+"F0.wireOp",EDGE,"E15.23.8"),sQuery(id+"F0.wireOp",EDGE,"E15.23.9"),sQuery(id+"F0.wireOp",EDGE,"E15.23.10"),sQuery(id+"F0.wireOp",EDGE,"E15.23.11"),sQuery(id+"F0.wireOp",EDGE,"E16.trimOffspring"),sQuery(id+"F0.wireOp",EDGE,"E17.trimOffspring"),sQuery(id+"F0.wireOp",EDGE,"E18.trimOffspring"),sQuery(id+"F0.wireOp",EDGE,"E19.trimOffspring"),sQuery(id+"F0.wireOp",EDGE,"E20.trimOffspring"),sQuery(id+"F0.wireOp",EDGE,"E21.trimOffspring"),sQuery(id+"F0.wireOp",EDGE,"E22.trimOffspring"),sQuery(id+"F0.wireOp",EDGE,"E23.trimOffspring"),sQuery(id+"F0.wireOp",EDGE,"E24.trimOffspring"),sQuery(id+"F0.wireOp",EDGE,"E25.trimOffspring"),sQuery(id+"F0.wireOp",EDGE,"E26.trimOffspring"),sQuery(id+"F0.wireOp",EDGE,"E27.trimOffspring"),sQuery(id+"F0.wireOp",EDGE,"E28.trimOffspring"),sQuery(id+"F0.wireOp",EDGE,"E29.trimOffspring"),sQuery(id+"F0.wireOp",EDGE,"E30.trimOffspring"),sQuery(id+"F0.wireOp",EDGE,"E31.trimOffspring"),sQuery(id+"F0.wireOp",EDGE,"E32.trimOffspring"),sQuery(id+"F0.wireOp",EDGE,"E33.trimOffspring"),sQuery(id+"F0.wireOp",EDGE,"E34.trimOffspring"),sQuery(id+"F0.wireOp",EDGE,"E35.trimOffspring"),sQuery(id+"F0.wireOp",EDGE,"E36.trimOffspring"),sQuery(id+"F0.wireOp",EDGE,"E37.trimOffspring"),sQuery(id+"F0.wireOp",EDGE,"E38.trimOffspring")])]});
            hole(context, id + "F3", {"style" : HoleStyle.SIMPLE, "endStyle" : HoleEndStyle.THROUGH, "holeDiameter" : 12.7 * mm, "tappedDepth" : 12.7 * mm, "tapClearance" : 3, "locations" : qUnion([Q0]), "scope" : qUnion([Q1])});
        }
    });
